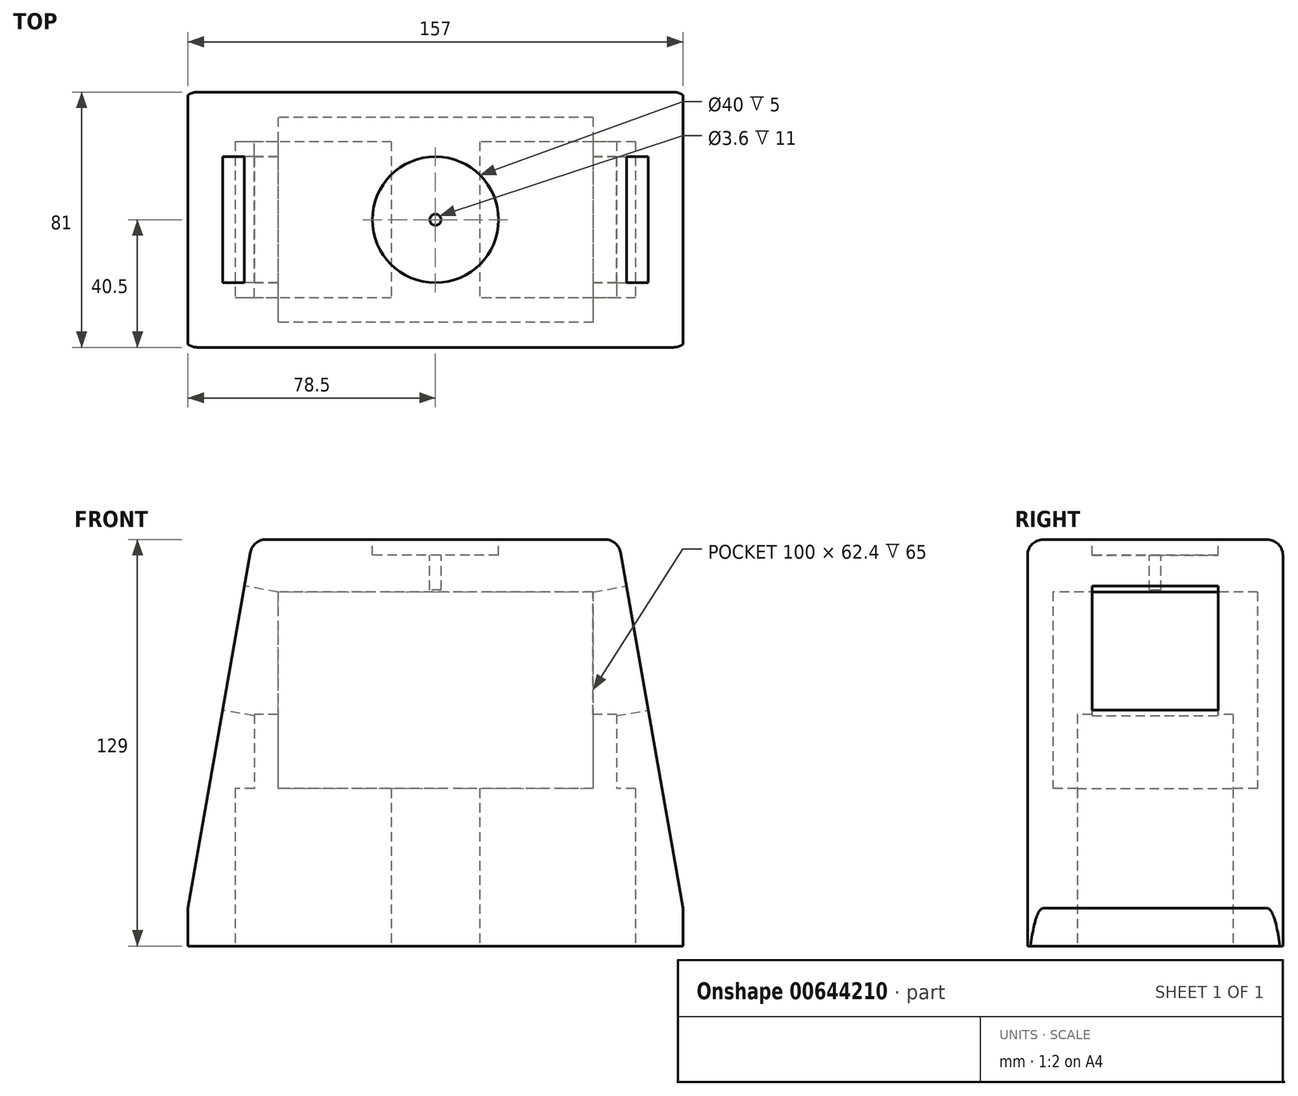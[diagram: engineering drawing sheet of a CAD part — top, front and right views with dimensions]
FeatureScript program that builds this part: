
annotation { "Feature Type Name" : "Feature", "Feature Type Description" : "" }
export const myFeature = defineFeature(function(context is Context, id is Id, definition is map)
    precondition{}
    {
        {
            var Q0;
            Q0=qCreatedBy(makeId("Top.planeOp"),FACE);
            var sketch = newSketch(context, id + "F0", { "sketchPlane" : qUnion([Q0])});
            skLineSegment(sketch, "E0.bottom", {"start": v(78.5, -40.5) * mm, "end": v(-78.5, -40.5) * mm});
            skLineSegment(sketch, "E0.top", {"start": v(78.5, 40.5) * mm, "end": v(-78.5, 40.5) * mm});
            skLineSegment(sketch, "E0.left", {"start": v(78.5, -40.5) * mm, "end": v(78.5, 40.5) * mm});
            skLineSegment(sketch, "E0.right", {"start": v(-78.5, -40.5) * mm, "end": v(-78.5, 40.5) * mm});
            skPoint(sketch, "E0.middle", {"position": v(0, 0) * mm});
            skSolve(sketch);
        }
        {
            var Q0;
            Q0=makeQuery(id+"F0.imprint","IMPRINT",FACE,{"disambiguationData":[TD([[makeQuery(id+"F0.imprint","IMPRINT",EDGE,{"derivedFrom":sQuery(id+"F0.wireOp",EDGE,"E0.bottom")}),-1.0]])]});
            extrude(context, id + "F1", {"entities" : qUnion([Q0]), "depth" : 12 * mm, "offsetDistance" : 25 * mm});
        }
        {
            var Q0;
            Q0=makeQuery(id+"F1.opExtrude","CAP_FACE",FACE,{"disambiguationData":[OSD([sQuery(id+"F0.wireOp",EDGE,"E0.bottom"),sQuery(id+"F0.wireOp",EDGE,"E0.top"),sQuery(id+"F0.wireOp",EDGE,"E0.left"),sQuery(id+"F0.wireOp",EDGE,"E0.right")])],"isStart":false});
            cPlane(context, id + "F2", {"entities" : qUnion([Q0]), "cplaneType" : CPlaneType.OFFSET, "offset" : 117 * mm, "width" : 150 * mm, "height" : 150 * mm});
        }
        {
            var Q0;
            Q0=qCreatedBy(id+"F2.planeOp",FACE);
            var sketch = newSketch(context, id + "F3", { "sketchPlane" : qUnion([Q0])});
            skLineSegment(sketch, "E1.bottom", {"start": v(58, -40.5) * mm, "end": v(-58, -40.5) * mm});
            skLineSegment(sketch, "E1.top", {"start": v(58, 40.5) * mm, "end": v(-58, 40.5) * mm});
            skLineSegment(sketch, "E1.left", {"start": v(58, -40.5) * mm, "end": v(58, 40.5) * mm});
            skLineSegment(sketch, "E1.right", {"start": v(-58, -40.5) * mm, "end": v(-58, 40.5) * mm});
            skPoint(sketch, "E1.middle", {"position": v(0, 0) * mm});
            skSolve(sketch);
        }
        {
            var Q1;
            Q1=makeQuery(id+"F1.opExtrude","CAP_FACE",FACE,{"disambiguationData":[OSD([sQuery(id+"F0.wireOp",EDGE,"E0.bottom"),sQuery(id+"F0.wireOp",EDGE,"E0.top"),sQuery(id+"F0.wireOp",EDGE,"E0.left"),sQuery(id+"F0.wireOp",EDGE,"E0.right")])],"isStart":false});
            var Q2;
            Q2=makeQuery(id+"F3.imprint","IMPRINT",FACE,{"disambiguationData":[TD([[makeQuery(id+"F3.imprint","IMPRINT",EDGE,{"derivedFrom":sQuery(id+"F3.wireOp",EDGE,"E1.bottom")}),-1.0]])]});
            loft(context, id + "F4", {"operationType" : NewBodyOperationType.ADD, "sheetProfilesArray" : [{ "sheetProfileEntities" : qUnion([Q1]) }, { "sheetProfileEntities" : qUnion([Q2]) }]});
        }
        {
            var Q0;
            Q0=makeQuery(id+"F1.opExtrude","CAP_FACE",FACE,{"disambiguationData":[OSD([sQuery(id+"F0.wireOp",EDGE,"E0.bottom"),sQuery(id+"F0.wireOp",EDGE,"E0.top"),sQuery(id+"F0.wireOp",EDGE,"E0.left"),sQuery(id+"F0.wireOp",EDGE,"E0.right")])],"isStart":true});
            var sketch = newSketch(context, id + "F5", { "sketchPlane" : qUnion([Q0])});
            skPoint(sketch, "E2", {"position": v(-38.75, 0) * mm});
            skPoint(sketch, "E3", {"position": v(38.75, 0) * mm});
            skLineSegment(sketch, "E4.bottom", {"start": v(-14, -24.75) * mm, "end": v(-63.5, -24.75) * mm});
            skLineSegment(sketch, "E4.top", {"start": v(-14, 24.75) * mm, "end": v(-63.5, 24.75) * mm});
            skLineSegment(sketch, "E4.left", {"start": v(-14, -24.75) * mm, "end": v(-14, 24.75) * mm});
            skLineSegment(sketch, "E4.right", {"start": v(-63.5, -24.75) * mm, "end": v(-63.5, 24.75) * mm});
            skLineSegment(sketch, "E5.bottom", {"start": v(63.5, -24.75) * mm, "end": v(14, -24.75) * mm});
            skLineSegment(sketch, "E5.top", {"start": v(63.5, 24.75) * mm, "end": v(14, 24.75) * mm});
            skLineSegment(sketch, "E5.left", {"start": v(63.5, -24.75) * mm, "end": v(63.5, 24.75) * mm});
            skLineSegment(sketch, "E5.right", {"start": v(14, -24.75) * mm, "end": v(14, 24.75) * mm});
            skPoint(sketch, "E6.middle", {"position": v(0, 0) * mm});
            skSolve(sketch);
        }
        {
            var Q0;
            Q0=makeQuery(id+"F5.imprint","IMPRINT",FACE,{"disambiguationData":[TD([[makeQuery(id+"F5.imprint","IMPRINT",EDGE,{"derivedFrom":sQuery(id+"F5.wireOp",EDGE,"E4.bottom")}),-1.0]])]});
            var Q1;
            Q1=makeQuery(id+"F5.imprint","IMPRINT",FACE,{"disambiguationData":[TD([[makeQuery(id+"F5.imprint","IMPRINT",EDGE,{"derivedFrom":sQuery(id+"F5.wireOp",EDGE,"E5.bottom")}),-1.0]])]});
            extrude(context, id + "F6", {"entities" : qUnion([Q0, Q1]), "operationType" : NewBodyOperationType.REMOVE, "oppositeDirection" : true, "depth" : 50 * mm, "offsetDistance" : 25 * mm});
        }
        {
            var Q0;
            Q0=makeQuery(id+"F6.boolean.opBoolean","COPY",FACE,{"derivedFrom":makeQuery(id+"F6.opExtrude","CAP_FACE",FACE,{"disambiguationData":[OSD([sQuery(id+"F5.wireOp",EDGE,"E4.bottom"),sQuery(id+"F5.wireOp",EDGE,"E4.top"),sQuery(id+"F5.wireOp",EDGE,"E4.left"),sQuery(id+"F5.wireOp",EDGE,"E4.right")])],"isStart":false})});
            var sketch = newSketch(context, id + "F7", { "sketchPlane" : qUnion([Q0])});
            skLineSegment(sketch, "E7.bottom", {"start": v(50, -32.5) * mm, "end": v(-50, -32.5) * mm});
            skLineSegment(sketch, "E7.top", {"start": v(50, 32.5) * mm, "end": v(-50, 32.5) * mm});
            skLineSegment(sketch, "E7.left", {"start": v(50, -32.5) * mm, "end": v(50, 32.5) * mm});
            skLineSegment(sketch, "E7.right", {"start": v(-50, -32.5) * mm, "end": v(-50, 32.5) * mm});
            skPoint(sketch, "E7.middle", {"position": v(0, 0) * mm});
            skSolve(sketch);
        }
        {
            var Q0;
            {var subQ5=makeQuery(id+"F6.boolean.opBoolean","COPY",EDGE,{"derivedFrom":makeQuery(id+"F6.opExtrude","CAP_EDGE",EDGE,{"disambiguationData":[OSD([sQuery(id+"F5.wireOp",EDGE,"E4.left")])],"isStart":false})});Q0=makeQuery(id+"F7.imprint","IMPRINT",FACE,{"disambiguationData":[TD([[makeQuery(id+"F7.imprint","IMPRINT",EDGE,{"derivedFrom":subQ5}),1.0]])]});}
            var Q1;
            {var subQ1=sQuery(id+"F7.wireOp",EDGE,"E7.bottom");Q1=makeQuery(id+"F7.imprint","IMPRINT",FACE,{"disambiguationData":[TD([[makeQuery(id+"F7.imprint","IMPRINT",EDGE,{"derivedFrom":subQ1}),-1.0]])]});}
            extrude(context, id + "F8", {"entities" : qUnion([Q0, Q1]), "operationType" : NewBodyOperationType.REMOVE, "oppositeDirection" : true, "depth" : 62.4 * mm, "offsetDistance" : 25 * mm});
        }
        {
            var Q0;
            Q0=makeQuery(id+"F4.opLoft","SWEPT_FACE",FACE,{"disambiguationData":[OSD([sQuery(id+"F0.wireOp",EDGE,"E0.bottom"),sQuery(id+"F0.wireOp",EDGE,"E0.top"),sQuery(id+"F0.wireOp",EDGE,"E0.left"),sQuery(id+"F3.wireOp",EDGE,"E1.bottom"),sQuery(id+"F3.wireOp",EDGE,"E1.top"),sQuery(id+"F3.wireOp",EDGE,"E1.left")])]});
            var sketch = newSketch(context, id + "F9", { "sketchPlane" : qUnion([Q0])});
            skLineSegment(sketch, "E8.bottom", {"start": v(25, 57.05) * mm, "end": v(-25, 57.05) * mm});
            skLineSegment(sketch, "E8.top", {"start": v(25, 107.05) * mm, "end": v(-25, 107.05) * mm});
            skLineSegment(sketch, "E8.left", {"start": v(25, 57.05) * mm, "end": v(25, 107.05) * mm});
            skLineSegment(sketch, "E8.right", {"start": v(-25, 57.05) * mm, "end": v(-25, 107.05) * mm});
            skPoint(sketch, "E8.middle", {"position": v(0, 82.05) * mm});
            skPoint(sketch, "E8.middle.positionSnap0", {"position": v(0, 117.05) * mm});
            skPoint(sketch, "E8.centerSnap0", {"position": v(0, 117.05) * mm});
            skSolve(sketch);
        }
        {
            var Q0;
            Q0=makeQuery(id+"F9.imprint","IMPRINT",FACE,{"disambiguationData":[TD([[makeQuery(id+"F9.imprint","IMPRINT",EDGE,{"derivedFrom":sQuery(id+"F9.wireOp",EDGE,"E8.bottom")}),-1.0]])]});
            extrude(context, id + "F10", {"entities" : qUnion([Q0]), "operationType" : NewBodyOperationType.REMOVE, "oppositeDirection" : true, "depth" : 10 * mm, "offsetDistance" : 25 * mm});
        }
        {
            var Q0;
            Q0=makeQuery(id+"F10.boolean.opBoolean","COPY",FACE,{"derivedFrom":makeQuery(id+"F10.opExtrude","CAP_FACE",FACE,{"disambiguationData":[OSD([sQuery(id+"F9.wireOp",EDGE,"E8.bottom"),sQuery(id+"F9.wireOp",EDGE,"E8.top"),sQuery(id+"F9.wireOp",EDGE,"E8.left"),sQuery(id+"F9.wireOp",EDGE,"E8.right")])],"isStart":false})});
            var sketch = newSketch(context, id + "F11", { "sketchPlane" : qUnion([Q0])});
            skLineSegment(sketch, "E9.bottom", {"start": v(20, 62.05) * mm, "end": v(-20, 62.05) * mm});
            skLineSegment(sketch, "E9.top", {"start": v(20, 102.05) * mm, "end": v(-20, 102.05) * mm});
            skLineSegment(sketch, "E9.left", {"start": v(20, 62.05) * mm, "end": v(20, 102.05) * mm});
            skLineSegment(sketch, "E9.right", {"start": v(-20, 62.05) * mm, "end": v(-20, 102.05) * mm});
            skPoint(sketch, "E9.middle", {"position": v(0, 82.05) * mm});
            skPoint(sketch, "E9.middle.positionSnap0", {"position": v(25, 82.05) * mm});
            skPoint(sketch, "E9.middle.positionSnap1", {"position": v(0, 107.05) * mm});
            skPoint(sketch, "E9.centerSnap0", {"position": v(25, 82.05) * mm});
            skPoint(sketch, "E9.centerSnap1", {"position": v(0, 107.05) * mm});
            skSolve(sketch);
        }
        {
            var Q0;
            Q0=makeQuery(id+"F11.imprint","IMPRINT",FACE,{"disambiguationData":[TD([[makeQuery(id+"F11.imprint","IMPRINT",EDGE,{"derivedFrom":sQuery(id+"F11.wireOp",EDGE,"E9.bottom")}),-1.0]])]});
            extrude(context, id + "F12", {"entities" : qUnion([Q0]), "operationType" : NewBodyOperationType.REMOVE, "oppositeDirection" : true, "depth" : 25 * mm, "offsetDistance" : 25 * mm});
        }
        {
            var Q0;
            Q0=makeQuery(id+"F10.boolean.opBoolean","COPY",FACE,{"derivedFrom":makeQuery(id+"F10.opExtrude","CAP_FACE",FACE,{"disambiguationData":[OSD([sQuery(id+"F9.wireOp",EDGE,"E8.bottom"),sQuery(id+"F9.wireOp",EDGE,"E8.top"),sQuery(id+"F9.wireOp",EDGE,"E8.left"),sQuery(id+"F9.wireOp",EDGE,"E8.right")])],"isStart":false})});
            var sketch = newSketch(context, id + "F13", { "sketchPlane" : qUnion([Q0])});
            skLineSegment(sketch, "E10.bottom", {"start": v(25, 57.05) * mm, "end": v(-25, 57.05) * mm});
            skLineSegment(sketch, "E10.top", {"start": v(25, 107.05) * mm, "end": v(-25, 107.05) * mm});
            skLineSegment(sketch, "E10.left", {"start": v(25, 57.05) * mm, "end": v(25, 107.05) * mm});
            skLineSegment(sketch, "E10.right", {"start": v(-25, 57.05) * mm, "end": v(-25, 107.05) * mm});
            skPoint(sketch, "E10.middle", {"position": v(0, 82.05) * mm});
            skPoint(sketch, "E10.middle.positionSnap0", {"position": v(20, 82.05) * mm});
            skPoint(sketch, "E10.middle.positionSnap1", {"position": v(0, 102.05) * mm});
            skPoint(sketch, "E10.centerSnap0", {"position": v(20, 82.05) * mm});
            skPoint(sketch, "E10.centerSnap1", {"position": v(0, 102.05) * mm});
            skSolve(sketch);
        }
        {
            var Q0;
            Q0=makeQuery(id+"F13.imprint","IMPRINT",FACE,{"disambiguationData":[TD([[makeQuery(id+"F13.imprint","IMPRINT",EDGE,{"derivedFrom":sQuery(id+"F13.wireOp",EDGE,"E10.bottom")}),-1.0]])]});
            var Q1;
            Q1=makeQuery(id+"F13.imprint","IMPRINT",FACE,{"disambiguationData":[TD([[makeQuery(id+"F13.imprint","IMPRINT",EDGE,{"derivedFrom":makeQuery(id+"F12.boolean.opBoolean","COPY",EDGE,{"derivedFrom":makeQuery(id+"F12.opExtrude","CAP_EDGE",EDGE,{"disambiguationData":[OSD([sQuery(id+"F11.wireOp",EDGE,"E9.bottom")])],"isStart":true})})}),-1.0]])]});
            extrude(context, id + "F14", {"entities" : qUnion([Q0, Q1]), "operationType" : NewBodyOperationType.ADD, "depth" : 10 * mm, "offsetDistance" : 25 * mm});
        }
        {
            var Q0;
            Q0=makeQuery(id+"F14.boolean.opBoolean","MERGE",FACE,{"derivedFrom":[makeQuery(id+"F4.opLoft","SWEPT_FACE",FACE,{"disambiguationData":[OSD([sQuery(id+"F0.wireOp",EDGE,"E0.bottom"),sQuery(id+"F0.wireOp",EDGE,"E0.top"),sQuery(id+"F0.wireOp",EDGE,"E0.left"),sQuery(id+"F3.wireOp",EDGE,"E1.bottom"),sQuery(id+"F3.wireOp",EDGE,"E1.top"),sQuery(id+"F3.wireOp",EDGE,"E1.left")])]}),makeQuery(id+"F14.opExtrude","CAP_FACE",FACE,{"disambiguationData":[OSD([sQuery(id+"F13.wireOp",EDGE,"E10.bottom"),sQuery(id+"F13.wireOp",EDGE,"E10.top"),sQuery(id+"F13.wireOp",EDGE,"E10.left"),sQuery(id+"F13.wireOp",EDGE,"E10.right")])],"isStart":false})]});
            var sketch = newSketch(context, id + "F15", { "sketchPlane" : qUnion([Q0])});
            skPoint(sketch, "E11", {"position": v(0, 82.05) * mm});
            skPoint(sketch, "E11.positionSnap0", {"position": v(0, 117.05) * mm});
            skCircle(sketch, "E12", {"center": v(0, 82.05) * mm, "radius": 12.5 * mm});
            skCircle(sketch, "E13", {"center": v(0, 82.05) * mm, "radius": 17.5 * mm});
            skLineSegment(sketch, "E14.bottom", {"start": v(-2.5, 82.05) * mm, "end": v(2.5, 82.05) * mm});
            skLineSegment(sketch, "E14.top", {"start": v(-2.5, 101.72) * mm, "end": v(2.5, 101.72) * mm});
            skLineSegment(sketch, "E14.left", {"start": v(-2.5, 82.05) * mm, "end": v(-2.5, 101.72) * mm});
            skLineSegment(sketch, "E14.right", {"start": v(2.5, 82.05) * mm, "end": v(2.5, 101.72) * mm});
            skLineSegment(sketch, "E15.1.0", {"start": v(-2.02, 80.58) * mm, "end": v(-13.58, 96.5) * mm});
            skLineSegment(sketch, "E15.1.1", {"start": v(2.02, 83.52) * mm, "end": v(-9.54, 99.43) * mm});
            skLineSegment(sketch, "E15.1.2", {"start": v(-13.58, 96.5) * mm, "end": v(-9.54, 99.43) * mm});
            skLineSegment(sketch, "E15.1.3", {"start": v(-2.02, 80.58) * mm, "end": v(2.02, 83.52) * mm});
            skLineSegment(sketch, "E15.2.0", {"start": v(-0.77, 79.68) * mm, "end": v(-19.48, 85.75) * mm});
            skLineSegment(sketch, "E15.2.1", {"start": v(0.77, 84.43) * mm, "end": v(-17.93, 90.5) * mm});
            skLineSegment(sketch, "E15.2.2", {"start": v(-19.48, 85.75) * mm, "end": v(-17.93, 90.5) * mm});
            skLineSegment(sketch, "E15.2.3", {"start": v(-0.77, 79.68) * mm, "end": v(0.77, 84.43) * mm});
            skLineSegment(sketch, "E15.3.0", {"start": v(0.77, 79.68) * mm, "end": v(-17.93, 73.6) * mm});
            skLineSegment(sketch, "E15.3.1", {"start": v(-0.77, 84.43) * mm, "end": v(-19.48, 78.36) * mm});
            skLineSegment(sketch, "E15.3.2", {"start": v(-17.93, 73.6) * mm, "end": v(-19.48, 78.36) * mm});
            skLineSegment(sketch, "E15.3.3", {"start": v(0.77, 79.68) * mm, "end": v(-0.77, 84.43) * mm});
            skLineSegment(sketch, "E15.4.0", {"start": v(2.02, 80.58) * mm, "end": v(-9.54, 64.68) * mm});
            skLineSegment(sketch, "E15.4.1", {"start": v(-2.02, 83.52) * mm, "end": v(-13.58, 67.61) * mm});
            skLineSegment(sketch, "E15.4.2", {"start": v(-9.54, 64.68) * mm, "end": v(-13.58, 67.61) * mm});
            skLineSegment(sketch, "E15.4.3", {"start": v(2.02, 80.58) * mm, "end": v(-2.02, 83.52) * mm});
            skLineSegment(sketch, "E15.5.0", {"start": v(2.5, 82.05) * mm, "end": v(2.5, 62.39) * mm});
            skLineSegment(sketch, "E15.5.1", {"start": v(-2.5, 82.05) * mm, "end": v(-2.5, 62.39) * mm});
            skLineSegment(sketch, "E15.5.2", {"start": v(2.5, 62.39) * mm, "end": v(-2.5, 62.39) * mm});
            skLineSegment(sketch, "E15.5.3", {"start": v(2.5, 82.05) * mm, "end": v(-2.5, 82.05) * mm});
            skLineSegment(sketch, "E15.6.0", {"start": v(2.02, 83.52) * mm, "end": v(13.58, 67.61) * mm});
            skLineSegment(sketch, "E15.6.1", {"start": v(-2.02, 80.58) * mm, "end": v(9.54, 64.68) * mm});
            skLineSegment(sketch, "E15.6.2", {"start": v(13.58, 67.61) * mm, "end": v(9.54, 64.68) * mm});
            skLineSegment(sketch, "E15.6.3", {"start": v(2.02, 83.52) * mm, "end": v(-2.02, 80.58) * mm});
            skLineSegment(sketch, "E15.7.0", {"start": v(0.77, 84.43) * mm, "end": v(19.48, 78.36) * mm});
            skLineSegment(sketch, "E15.7.1", {"start": v(-0.77, 79.68) * mm, "end": v(17.93, 73.6) * mm});
            skLineSegment(sketch, "E15.7.2", {"start": v(19.48, 78.36) * mm, "end": v(17.93, 73.6) * mm});
            skLineSegment(sketch, "E15.7.3", {"start": v(0.77, 84.43) * mm, "end": v(-0.77, 79.68) * mm});
            skLineSegment(sketch, "E15.8.0", {"start": v(-0.77, 84.43) * mm, "end": v(17.93, 90.5) * mm});
            skLineSegment(sketch, "E15.8.1", {"start": v(0.77, 79.68) * mm, "end": v(19.48, 85.75) * mm});
            skLineSegment(sketch, "E15.8.2", {"start": v(17.93, 90.5) * mm, "end": v(19.48, 85.75) * mm});
            skLineSegment(sketch, "E15.8.3", {"start": v(-0.77, 84.43) * mm, "end": v(0.77, 79.68) * mm});
            skLineSegment(sketch, "E15.9.0", {"start": v(-2.02, 83.52) * mm, "end": v(9.54, 99.43) * mm});
            skLineSegment(sketch, "E15.9.1", {"start": v(2.02, 80.58) * mm, "end": v(13.58, 96.5) * mm});
            skLineSegment(sketch, "E15.9.2", {"start": v(9.54, 99.43) * mm, "end": v(13.58, 96.5) * mm});
            skLineSegment(sketch, "E15.9.3", {"start": v(-2.02, 83.52) * mm, "end": v(2.02, 80.58) * mm});
            skSolve(sketch);
        }
        {
            var Q0;
            {var subQ0=sQuery(id+"F15.wireOp",EDGE,"E14.right");var subQ1=sQuery(id+"F15.wireOp",EDGE,"E12");var subQ2=makeQuery(id+"F15.imprint","INTERSECT",VERTEX,{"derivedFrom":[subQ1,subQ0]});Q0=makeQuery(id+"F15.imprint","IMPRINT",FACE,{"disambiguationData":[TD([[makeQuery(id+"F15.imprint","IMPRINT",EDGE,{"disambiguationData":[TD([[subQ2,-1.0]])],"derivedFrom":subQ1}),-1.0]])]});}
            var Q1;
            {var subQ0=sQuery(id+"F15.wireOp",EDGE,"E14.right");var subQ1=sQuery(id+"F15.wireOp",EDGE,"E12");var subQ2=makeQuery(id+"F15.imprint","INTERSECT",VERTEX,{"derivedFrom":[subQ1,subQ0]});Q1=makeQuery(id+"F15.imprint","IMPRINT",FACE,{"disambiguationData":[TD([[makeQuery(id+"F15.imprint","IMPRINT",EDGE,{"disambiguationData":[TD([[subQ2,-1.0]])],"derivedFrom":subQ1}),1.0]])]});}
            var Q2;
            {var subQ0=sQuery(id+"F15.wireOp",EDGE,"E15.4.1");var subQ1=sQuery(id+"F15.wireOp",EDGE,"E12");var subQ2=makeQuery(id+"F15.imprint","INTERSECT",VERTEX,{"derivedFrom":[subQ1,subQ0]});Q2=makeQuery(id+"F15.imprint","IMPRINT",FACE,{"disambiguationData":[TD([[makeQuery(id+"F15.imprint","IMPRINT",EDGE,{"disambiguationData":[TD([[subQ2,-1.0]])],"derivedFrom":subQ1}),1.0]])]});}
            var Q3;
            {var subQ0=sQuery(id+"F15.wireOp",EDGE,"E15.4.1");var subQ1=sQuery(id+"F15.wireOp",EDGE,"E12");var subQ2=makeQuery(id+"F15.imprint","INTERSECT",VERTEX,{"derivedFrom":[subQ1,subQ0]});Q3=makeQuery(id+"F15.imprint","IMPRINT",FACE,{"disambiguationData":[TD([[makeQuery(id+"F15.imprint","IMPRINT",EDGE,{"disambiguationData":[TD([[subQ2,-1.0]])],"derivedFrom":subQ1}),-1.0]])]});}
            var Q4;
            {var subQ0=sQuery(id+"F15.wireOp",EDGE,"E15.6.1");var subQ1=sQuery(id+"F15.wireOp",EDGE,"E12");var subQ2=makeQuery(id+"F15.imprint","INTERSECT",VERTEX,{"derivedFrom":[subQ1,subQ0]});Q4=makeQuery(id+"F15.imprint","IMPRINT",FACE,{"disambiguationData":[TD([[makeQuery(id+"F15.imprint","IMPRINT",EDGE,{"disambiguationData":[TD([[subQ2,-1.0]])],"derivedFrom":subQ1}),-1.0]])]});}
            var Q5;
            {var subQ0=sQuery(id+"F15.wireOp",EDGE,"E15.6.1");var subQ1=sQuery(id+"F15.wireOp",EDGE,"E12");var subQ2=makeQuery(id+"F15.imprint","INTERSECT",VERTEX,{"derivedFrom":[subQ1,subQ0]});Q5=makeQuery(id+"F15.imprint","IMPRINT",FACE,{"disambiguationData":[TD([[makeQuery(id+"F15.imprint","IMPRINT",EDGE,{"disambiguationData":[TD([[subQ2,-1.0]])],"derivedFrom":subQ1}),1.0]])]});}
            var Q6;
            {var subQ0=sQuery(id+"F15.wireOp",EDGE,"E15.5.1");var subQ1=sQuery(id+"F15.wireOp",EDGE,"E12");var subQ2=makeQuery(id+"F15.imprint","INTERSECT",VERTEX,{"derivedFrom":[subQ1,subQ0]});Q6=makeQuery(id+"F15.imprint","IMPRINT",FACE,{"disambiguationData":[TD([[makeQuery(id+"F15.imprint","IMPRINT",EDGE,{"disambiguationData":[TD([[subQ2,-1.0]])],"derivedFrom":subQ1}),1.0]])]});}
            var Q7;
            {var subQ0=sQuery(id+"F15.wireOp",EDGE,"E15.4.0");var subQ1=sQuery(id+"F15.wireOp",EDGE,"E12");var subQ2=makeQuery(id+"F15.imprint","INTERSECT",VERTEX,{"derivedFrom":[subQ1,subQ0]});Q7=makeQuery(id+"F15.imprint","IMPRINT",FACE,{"disambiguationData":[TD([[makeQuery(id+"F15.imprint","IMPRINT",EDGE,{"disambiguationData":[TD([[subQ2,-1.0]])],"derivedFrom":subQ1}),1.0]])]});}
            var Q8;
            {var subQ0=sQuery(id+"F15.wireOp",EDGE,"E15.5.0");var subQ1=sQuery(id+"F15.wireOp",EDGE,"E12");var subQ2=makeQuery(id+"F15.imprint","INTERSECT",VERTEX,{"derivedFrom":[subQ1,subQ0]});Q8=makeQuery(id+"F15.imprint","IMPRINT",FACE,{"disambiguationData":[TD([[makeQuery(id+"F15.imprint","IMPRINT",EDGE,{"disambiguationData":[TD([[subQ2,-1.0]])],"derivedFrom":subQ1}),1.0]])]});}
            var Q9;
            {var subQ0=sQuery(id+"F15.wireOp",EDGE,"E15.6.0");var subQ1=sQuery(id+"F15.wireOp",EDGE,"E12");var subQ2=makeQuery(id+"F15.imprint","INTERSECT",VERTEX,{"derivedFrom":[subQ1,subQ0]});Q9=makeQuery(id+"F15.imprint","IMPRINT",FACE,{"disambiguationData":[TD([[makeQuery(id+"F15.imprint","IMPRINT",EDGE,{"disambiguationData":[TD([[subQ2,-1.0]])],"derivedFrom":subQ1}),1.0]])]});}
            var Q10;
            {var subQ0=sQuery(id+"F15.wireOp",EDGE,"E15.7.1");var subQ1=sQuery(id+"F15.wireOp",EDGE,"E12");var subQ2=makeQuery(id+"F15.imprint","INTERSECT",VERTEX,{"derivedFrom":[subQ1,subQ0]});Q10=makeQuery(id+"F15.imprint","IMPRINT",FACE,{"disambiguationData":[TD([[makeQuery(id+"F15.imprint","IMPRINT",EDGE,{"disambiguationData":[TD([[subQ2,-1.0]])],"derivedFrom":subQ1}),1.0]])]});}
            var Q11;
            {var subQ0=sQuery(id+"F15.wireOp",EDGE,"E15.8.1");var subQ1=sQuery(id+"F15.wireOp",EDGE,"E12");var subQ2=makeQuery(id+"F15.imprint","INTERSECT",VERTEX,{"derivedFrom":[subQ1,subQ0]});Q11=makeQuery(id+"F15.imprint","IMPRINT",FACE,{"disambiguationData":[TD([[makeQuery(id+"F15.imprint","IMPRINT",EDGE,{"disambiguationData":[TD([[subQ2,1.0]])],"derivedFrom":subQ1}),1.0]])]});}
            var Q12;
            {var subQ1=sQuery(id+"F15.wireOp",EDGE,"E12");var subQ7=sQuery(id+"F15.wireOp",EDGE,"E15.8.0");var subQ8=makeQuery(id+"F15.imprint","INTERSECT",VERTEX,{"derivedFrom":[subQ1,subQ7]});Q12=makeQuery(id+"F15.imprint","IMPRINT",FACE,{"disambiguationData":[TD([[makeQuery(id+"F15.imprint","IMPRINT",EDGE,{"disambiguationData":[TD([[subQ8,1.0]])],"derivedFrom":subQ1}),1.0]])]});}
            var Q13;
            {var subQ3=sQuery(id+"F15.wireOp",EDGE,"E15.9.1");var subQ7=sQuery(id+"F15.wireOp",EDGE,"E12");var subQ8=makeQuery(id+"F15.imprint","INTERSECT",VERTEX,{"derivedFrom":[subQ7,subQ3]});Q13=makeQuery(id+"F15.imprint","IMPRINT",FACE,{"disambiguationData":[TD([[makeQuery(id+"F15.imprint","IMPRINT",EDGE,{"disambiguationData":[TD([[subQ8,-1.0]])],"derivedFrom":subQ7}),1.0]])]});}
            var Q14;
            {var subQ0=sQuery(id+"F15.wireOp",EDGE,"E15.8.0");var subQ1=sQuery(id+"F15.wireOp",EDGE,"E12");var subQ2=makeQuery(id+"F15.imprint","INTERSECT",VERTEX,{"derivedFrom":[subQ1,subQ0]});Q14=makeQuery(id+"F15.imprint","IMPRINT",FACE,{"disambiguationData":[TD([[makeQuery(id+"F15.imprint","IMPRINT",EDGE,{"disambiguationData":[TD([[subQ2,-1.0]])],"derivedFrom":subQ1}),1.0]])]});}
            var Q15;
            {var subQ0=sQuery(id+"F15.wireOp",EDGE,"E15.9.0");var subQ1=sQuery(id+"F15.wireOp",EDGE,"E12");var subQ2=makeQuery(id+"F15.imprint","INTERSECT",VERTEX,{"derivedFrom":[subQ1,subQ0]});Q15=makeQuery(id+"F15.imprint","IMPRINT",FACE,{"disambiguationData":[TD([[makeQuery(id+"F15.imprint","IMPRINT",EDGE,{"disambiguationData":[TD([[subQ2,-1.0]])],"derivedFrom":subQ1}),1.0]])]});}
            var Q16;
            {var subQ0=sQuery(id+"F15.wireOp",EDGE,"E14.left");var subQ1=sQuery(id+"F15.wireOp",EDGE,"E12");var subQ2=makeQuery(id+"F15.imprint","INTERSECT",VERTEX,{"derivedFrom":[subQ1,subQ0]});Q16=makeQuery(id+"F15.imprint","IMPRINT",FACE,{"disambiguationData":[TD([[makeQuery(id+"F15.imprint","IMPRINT",EDGE,{"disambiguationData":[TD([[subQ2,-1.0]])],"derivedFrom":subQ1}),1.0]])]});}
            var Q17;
            {var subQ1=sQuery(id+"F15.wireOp",EDGE,"E12");var subQ7=sQuery(id+"F15.wireOp",EDGE,"E15.1.1");var subQ9=makeQuery(id+"F15.imprint","INTERSECT",VERTEX,{"derivedFrom":[subQ1,subQ7]});Q17=makeQuery(id+"F15.imprint","IMPRINT",FACE,{"disambiguationData":[TD([[makeQuery(id+"F15.imprint","IMPRINT",EDGE,{"disambiguationData":[TD([[subQ9,-1.0]])],"derivedFrom":subQ1}),1.0]])]});}
            var Q18;
            {var subQ0=sQuery(id+"F15.wireOp",EDGE,"E15.1.0");var subQ1=sQuery(id+"F15.wireOp",EDGE,"E12");var subQ2=makeQuery(id+"F15.imprint","INTERSECT",VERTEX,{"derivedFrom":[subQ1,subQ0]});Q18=makeQuery(id+"F15.imprint","IMPRINT",FACE,{"disambiguationData":[TD([[makeQuery(id+"F15.imprint","IMPRINT",EDGE,{"disambiguationData":[TD([[subQ2,-1.0]])],"derivedFrom":subQ1}),1.0]])]});}
            var Q19;
            {var subQ0=sQuery(id+"F15.wireOp",EDGE,"E15.2.1");var subQ1=sQuery(id+"F15.wireOp",EDGE,"E12");var subQ2=makeQuery(id+"F15.imprint","INTERSECT",VERTEX,{"derivedFrom":[subQ1,subQ0]});Q19=makeQuery(id+"F15.imprint","IMPRINT",FACE,{"disambiguationData":[TD([[makeQuery(id+"F15.imprint","IMPRINT",EDGE,{"disambiguationData":[TD([[subQ2,-1.0]])],"derivedFrom":subQ1}),1.0]])]});}
            var Q20;
            {var subQ0=sQuery(id+"F15.wireOp",EDGE,"E15.2.0");var subQ1=sQuery(id+"F15.wireOp",EDGE,"E12");var subQ2=makeQuery(id+"F15.imprint","INTERSECT",VERTEX,{"derivedFrom":[subQ1,subQ0]});Q20=makeQuery(id+"F15.imprint","IMPRINT",FACE,{"disambiguationData":[TD([[makeQuery(id+"F15.imprint","IMPRINT",EDGE,{"disambiguationData":[TD([[subQ2,-1.0]])],"derivedFrom":subQ1}),1.0]])]});}
            var Q21;
            {var subQ0=sQuery(id+"F15.wireOp",EDGE,"E15.3.0");var subQ1=sQuery(id+"F15.wireOp",EDGE,"E12");var subQ2=makeQuery(id+"F15.imprint","INTERSECT",VERTEX,{"derivedFrom":[subQ1,subQ0]});Q21=makeQuery(id+"F15.imprint","IMPRINT",FACE,{"disambiguationData":[TD([[makeQuery(id+"F15.imprint","IMPRINT",EDGE,{"disambiguationData":[TD([[subQ2,-1.0]])],"derivedFrom":subQ1}),1.0]])]});}
            var Q22;
            {var subQ0=sQuery(id+"F15.wireOp",EDGE,"E15.3.1");var subQ1=sQuery(id+"F15.wireOp",EDGE,"E12");var subQ2=makeQuery(id+"F15.imprint","INTERSECT",VERTEX,{"derivedFrom":[subQ1,subQ0]});Q22=makeQuery(id+"F15.imprint","IMPRINT",FACE,{"disambiguationData":[TD([[makeQuery(id+"F15.imprint","IMPRINT",EDGE,{"disambiguationData":[TD([[subQ2,-1.0]])],"derivedFrom":subQ1}),1.0]])]});}
            var Q23;
            {var subQ0=sQuery(id+"F15.wireOp",EDGE,"E15.8.1");var subQ1=sQuery(id+"F15.wireOp",EDGE,"E15.4.0");var subQ2=makeQuery(id+"F15.imprint","INTERSECT",VERTEX,{"derivedFrom":[subQ1,subQ0]});Q23=makeQuery(id+"F15.imprint","IMPRINT",FACE,{"disambiguationData":[TD([[makeQuery(id+"F15.imprint","IMPRINT",EDGE,{"disambiguationData":[TD([[subQ2,-1.0]])],"derivedFrom":subQ1}),1.0]])]});}
            var Q24;
            {var subQ1=sQuery(id+"F15.wireOp",EDGE,"E15.1.1");var subQ3=sQuery(id+"F15.wireOp",EDGE,"E15.7.0");var subQ4=makeQuery(id+"F15.imprint","INTERSECT",VERTEX,{"derivedFrom":[subQ1,subQ3]});Q24=makeQuery(id+"F15.imprint","IMPRINT",FACE,{"disambiguationData":[TD([[makeQuery(id+"F15.imprint","IMPRINT",EDGE,{"disambiguationData":[TD([[subQ4,1.0]])],"derivedFrom":subQ1}),1.0]])]});}
            var Q25;
            {var subQ0=sQuery(id+"F15.wireOp",EDGE,"E15.7.1");var subQ1=sQuery(id+"F15.wireOp",EDGE,"E15.4.0");var subQ2=makeQuery(id+"F15.imprint","INTERSECT",VERTEX,{"derivedFrom":[subQ1,subQ0]});Q25=makeQuery(id+"F15.imprint","IMPRINT",FACE,{"disambiguationData":[TD([[makeQuery(id+"F15.imprint","IMPRINT",EDGE,{"disambiguationData":[TD([[subQ2,-1.0]])],"derivedFrom":subQ1}),1.0]])]});}
            var Q26;
            {var subQ0=sQuery(id+"F15.wireOp",EDGE,"E15.4.1");var subQ1=sQuery(id+"F15.wireOp",EDGE,"E14.left");var subQ2=makeQuery(id+"F15.imprint","INTERSECT",VERTEX,{"derivedFrom":[subQ1,subQ0]});Q26=makeQuery(id+"F15.imprint","IMPRINT",FACE,{"disambiguationData":[TD([[makeQuery(id+"F15.imprint","IMPRINT",EDGE,{"disambiguationData":[TD([[subQ2,-1.0]])],"derivedFrom":subQ1}),1.0]])]});}
            var Q27;
            {var subQ0=sQuery(id+"F15.wireOp",EDGE,"E15.6.0");var subQ1=sQuery(id+"F15.wireOp",EDGE,"E14.right");var subQ2=makeQuery(id+"F15.imprint","INTERSECT",VERTEX,{"derivedFrom":[subQ1,subQ0]});Q27=makeQuery(id+"F15.imprint","IMPRINT",FACE,{"disambiguationData":[TD([[makeQuery(id+"F15.imprint","IMPRINT",EDGE,{"disambiguationData":[TD([[subQ2,-1.0]])],"derivedFrom":subQ1}),-1.0]])]});}
            var Q28;
            {var subQ0=sQuery(id+"F15.wireOp",EDGE,"E15.8.1");var subQ1=sQuery(id+"F15.wireOp",EDGE,"E15.5.0");var subQ2=makeQuery(id+"F15.imprint","INTERSECT",VERTEX,{"derivedFrom":[subQ1,subQ0]});Q28=makeQuery(id+"F15.imprint","IMPRINT",FACE,{"disambiguationData":[TD([[makeQuery(id+"F15.imprint","IMPRINT",EDGE,{"disambiguationData":[TD([[subQ2,-1.0]])],"derivedFrom":subQ1}),1.0]])]});}
            var Q29;
            {var subQ0=sQuery(id+"F15.wireOp",EDGE,"E15.2.1");var subQ1=sQuery(id+"F15.wireOp",EDGE,"E14.left");var subQ2=makeQuery(id+"F15.imprint","INTERSECT",VERTEX,{"derivedFrom":[subQ1,subQ0]});Q29=makeQuery(id+"F15.imprint","IMPRINT",FACE,{"disambiguationData":[TD([[makeQuery(id+"F15.imprint","IMPRINT",EDGE,{"disambiguationData":[TD([[subQ2,-1.0]])],"derivedFrom":subQ1}),-1.0]])]});}
            var Q30;
            {var subQ0=sQuery(id+"F15.wireOp",EDGE,"E15.4.1");var subQ1=sQuery(id+"F15.wireOp",EDGE,"E14.left");var subQ2=makeQuery(id+"F15.imprint","INTERSECT",VERTEX,{"derivedFrom":[subQ1,subQ0]});Q30=makeQuery(id+"F15.imprint","IMPRINT",FACE,{"disambiguationData":[TD([[makeQuery(id+"F15.imprint","IMPRINT",EDGE,{"disambiguationData":[TD([[subQ2,-1.0]])],"derivedFrom":subQ1}),-1.0]])]});}
            var Q31;
            {var subQ0=sQuery(id+"F15.wireOp",EDGE,"E15.7.0");var subQ1=sQuery(id+"F15.wireOp",EDGE,"E15.1.1");var subQ2=makeQuery(id+"F15.imprint","INTERSECT",VERTEX,{"derivedFrom":[subQ1,subQ0]});Q31=makeQuery(id+"F15.imprint","IMPRINT",FACE,{"disambiguationData":[TD([[makeQuery(id+"F15.imprint","IMPRINT",EDGE,{"disambiguationData":[TD([[subQ2,-1.0]])],"derivedFrom":subQ1}),1.0]])]});}
            var Q32;
            {var subQ1=sQuery(id+"F15.wireOp",EDGE,"E15.5.0");var subQ3=sQuery(id+"F15.wireOp",EDGE,"E15.9.1");var subQ4=makeQuery(id+"F15.imprint","INTERSECT",VERTEX,{"derivedFrom":[subQ1,subQ3]});Q32=makeQuery(id+"F15.imprint","IMPRINT",FACE,{"disambiguationData":[TD([[makeQuery(id+"F15.imprint","IMPRINT",EDGE,{"disambiguationData":[TD([[subQ4,1.0]])],"derivedFrom":subQ1}),-1.0]])]});}
            var Q33;
            {var subQ0=sQuery(id+"F15.wireOp",EDGE,"E15.8.0");var subQ1=sQuery(id+"F15.wireOp",EDGE,"E14.right");var subQ2=makeQuery(id+"F15.imprint","INTERSECT",VERTEX,{"derivedFrom":[subQ1,subQ0]});Q33=makeQuery(id+"F15.imprint","IMPRINT",FACE,{"disambiguationData":[TD([[makeQuery(id+"F15.imprint","IMPRINT",EDGE,{"disambiguationData":[TD([[subQ2,-1.0]])],"derivedFrom":subQ1}),1.0]])]});}
            var Q34;
            {var subQ0=sQuery(id+"F15.wireOp",EDGE,"E15.6.1");var subQ5=sQuery(id+"F15.wireOp",EDGE,"E15.2.0");var subQ6=makeQuery(id+"F15.imprint","INTERSECT",VERTEX,{"derivedFrom":[subQ5,subQ0]});Q34=makeQuery(id+"F15.imprint","IMPRINT",FACE,{"disambiguationData":[TD([[makeQuery(id+"F15.imprint","IMPRINT",EDGE,{"disambiguationData":[TD([[subQ6,-1.0]])],"derivedFrom":subQ5}),-1.0]])]});}
            var Q35;
            {var subQ0=sQuery(id+"F15.wireOp",EDGE,"E15.9.1");var subQ1=sQuery(id+"F15.wireOp",EDGE,"E15.5.0");var subQ2=makeQuery(id+"F15.imprint","INTERSECT",VERTEX,{"derivedFrom":[subQ1,subQ0]});Q35=makeQuery(id+"F15.imprint","IMPRINT",FACE,{"disambiguationData":[TD([[makeQuery(id+"F15.imprint","IMPRINT",EDGE,{"disambiguationData":[TD([[subQ2,-1.0]])],"derivedFrom":subQ1}),1.0]])]});}
            var Q36;
            {var subQ1=sQuery(id+"F15.wireOp",EDGE,"E15.3.0");var subQ3=sQuery(id+"F15.wireOp",EDGE,"E15.7.1");var subQ4=makeQuery(id+"F15.imprint","INTERSECT",VERTEX,{"derivedFrom":[subQ1,subQ3]});Q36=makeQuery(id+"F15.imprint","IMPRINT",FACE,{"disambiguationData":[TD([[makeQuery(id+"F15.imprint","IMPRINT",EDGE,{"disambiguationData":[TD([[subQ4,1.0]])],"derivedFrom":subQ1}),-1.0]])]});}
            var Q37;
            {var subQ0=sQuery(id+"F15.wireOp",EDGE,"E15.7.0");var subQ1=sQuery(id+"F15.wireOp",EDGE,"E14.right");var subQ2=makeQuery(id+"F15.imprint","INTERSECT",VERTEX,{"derivedFrom":[subQ1,subQ0]});Q37=makeQuery(id+"F15.imprint","IMPRINT",FACE,{"disambiguationData":[TD([[makeQuery(id+"F15.imprint","IMPRINT",EDGE,{"disambiguationData":[TD([[subQ2,-1.0]])],"derivedFrom":subQ1}),-1.0]])]});}
            var Q38;
            {var subQ0=sQuery(id+"F15.wireOp",EDGE,"E15.6.1");var subQ1=sQuery(id+"F15.wireOp",EDGE,"E15.3.0");var subQ2=makeQuery(id+"F15.imprint","INTERSECT",VERTEX,{"derivedFrom":[subQ1,subQ0]});Q38=makeQuery(id+"F15.imprint","IMPRINT",FACE,{"disambiguationData":[TD([[makeQuery(id+"F15.imprint","IMPRINT",EDGE,{"disambiguationData":[TD([[subQ2,-1.0]])],"derivedFrom":subQ1}),1.0]])]});}
            var Q39;
            {var subQ0=sQuery(id+"F15.wireOp",EDGE,"E15.7.1");var subQ1=sQuery(id+"F15.wireOp",EDGE,"E15.3.0");var subQ2=makeQuery(id+"F15.imprint","INTERSECT",VERTEX,{"derivedFrom":[subQ1,subQ0]});Q39=makeQuery(id+"F15.imprint","IMPRINT",FACE,{"disambiguationData":[TD([[makeQuery(id+"F15.imprint","IMPRINT",EDGE,{"disambiguationData":[TD([[subQ2,-1.0]])],"derivedFrom":subQ1}),1.0]])]});}
            var Q40;
            {var subQ1=sQuery(id+"F15.wireOp",EDGE,"E15.4.0");var subQ3=sQuery(id+"F15.wireOp",EDGE,"E15.8.1");var subQ4=makeQuery(id+"F15.imprint","INTERSECT",VERTEX,{"derivedFrom":[subQ1,subQ3]});Q40=makeQuery(id+"F15.imprint","IMPRINT",FACE,{"disambiguationData":[TD([[makeQuery(id+"F15.imprint","IMPRINT",EDGE,{"disambiguationData":[TD([[subQ4,1.0]])],"derivedFrom":subQ1}),-1.0]])]});}
            var Q41;
            {var subQ1=sQuery(id+"F15.wireOp",EDGE,"E14.right");var subQ3=sQuery(id+"F15.wireOp",EDGE,"E15.6.0");var subQ4=makeQuery(id+"F15.imprint","INTERSECT",VERTEX,{"derivedFrom":[subQ1,subQ3]});Q41=makeQuery(id+"F15.imprint","IMPRINT",FACE,{"disambiguationData":[TD([[makeQuery(id+"F15.imprint","IMPRINT",EDGE,{"disambiguationData":[TD([[subQ4,-1.0]])],"derivedFrom":subQ3}),-1.0]])]});}
            var Q42;
            {var subQ1=sQuery(id+"F15.wireOp",EDGE,"E14.left");var subQ3=sQuery(id+"F15.wireOp",EDGE,"E15.4.1");var subQ4=makeQuery(id+"F15.imprint","INTERSECT",VERTEX,{"derivedFrom":[subQ1,subQ3]});Q42=makeQuery(id+"F15.imprint","IMPRINT",FACE,{"disambiguationData":[TD([[makeQuery(id+"F15.imprint","IMPRINT",EDGE,{"disambiguationData":[TD([[subQ4,1.0]])],"derivedFrom":subQ1}),-1.0]])]});}
            var Q43;
            {var subQ1=sQuery(id+"F15.wireOp",EDGE,"E15.1.0");var subQ3=sQuery(id+"F15.wireOp",EDGE,"E15.5.1");var subQ4=makeQuery(id+"F15.imprint","INTERSECT",VERTEX,{"derivedFrom":[subQ1,subQ3]});Q43=makeQuery(id+"F15.imprint","IMPRINT",FACE,{"disambiguationData":[TD([[makeQuery(id+"F15.imprint","IMPRINT",EDGE,{"disambiguationData":[TD([[subQ4,1.0]])],"derivedFrom":subQ1}),-1.0]])]});}
            var Q44;
            {var subQ0=sQuery(id+"F15.wireOp",EDGE,"E15.5.1");var subQ5=sQuery(id+"F15.wireOp",EDGE,"E15.1.0");var subQ6=makeQuery(id+"F15.imprint","INTERSECT",VERTEX,{"derivedFrom":[subQ5,subQ0]});Q44=makeQuery(id+"F15.imprint","IMPRINT",FACE,{"disambiguationData":[TD([[makeQuery(id+"F15.imprint","IMPRINT",EDGE,{"disambiguationData":[TD([[subQ6,-1.0]])],"derivedFrom":subQ5}),-1.0]])]});}
            var Q45;
            {var subQ0=sQuery(id+"F15.wireOp",EDGE,"E15.5.1");var subQ1=sQuery(id+"F15.wireOp",EDGE,"E15.2.0");var subQ2=makeQuery(id+"F15.imprint","INTERSECT",VERTEX,{"derivedFrom":[subQ1,subQ0]});Q45=makeQuery(id+"F15.imprint","IMPRINT",FACE,{"disambiguationData":[TD([[makeQuery(id+"F15.imprint","IMPRINT",EDGE,{"disambiguationData":[TD([[subQ2,-1.0]])],"derivedFrom":subQ1}),1.0]])]});}
            var Q46;
            {var subQ0=sQuery(id+"F15.wireOp",EDGE,"E15.6.1");var subQ1=sQuery(id+"F15.wireOp",EDGE,"E15.2.0");var subQ2=makeQuery(id+"F15.imprint","INTERSECT",VERTEX,{"derivedFrom":[subQ1,subQ0]});Q46=makeQuery(id+"F15.imprint","IMPRINT",FACE,{"disambiguationData":[TD([[makeQuery(id+"F15.imprint","IMPRINT",EDGE,{"disambiguationData":[TD([[subQ2,-1.0]])],"derivedFrom":subQ1}),1.0]])]});}
            var Q47;
            {var subQ0=sQuery(id+"F15.wireOp",EDGE,"E15.9.1");var subQ1=sQuery(id+"F15.wireOp",EDGE,"E15.6.0");var subQ2=makeQuery(id+"F15.imprint","INTERSECT",VERTEX,{"derivedFrom":[subQ1,subQ0]});Q47=makeQuery(id+"F15.imprint","IMPRINT",FACE,{"disambiguationData":[TD([[makeQuery(id+"F15.imprint","IMPRINT",EDGE,{"disambiguationData":[TD([[subQ2,-1.0]])],"derivedFrom":subQ1}),1.0]])]});}
            var Q48;
            {var subQ0=sQuery(id+"F15.wireOp",EDGE,"E15.7.1");var subQ5=sQuery(id+"F15.wireOp",EDGE,"E15.3.0");var subQ7=makeQuery(id+"F15.imprint","INTERSECT",VERTEX,{"derivedFrom":[subQ5,subQ0]});Q48=makeQuery(id+"F15.imprint","IMPRINT",FACE,{"disambiguationData":[TD([[makeQuery(id+"F15.imprint","IMPRINT",EDGE,{"disambiguationData":[TD([[subQ7,-1.0]])],"derivedFrom":subQ5}),-1.0]])]});}
            var Q49;
            {var subQ0=sQuery(id+"F15.wireOp",EDGE,"E15.8.0");var subQ1=sQuery(id+"F15.wireOp",EDGE,"E15.1.1");var subQ2=makeQuery(id+"F15.imprint","INTERSECT",VERTEX,{"derivedFrom":[subQ1,subQ0]});Q49=makeQuery(id+"F15.imprint","IMPRINT",FACE,{"disambiguationData":[TD([[makeQuery(id+"F15.imprint","IMPRINT",EDGE,{"disambiguationData":[TD([[subQ2,-1.0]])],"derivedFrom":subQ1}),1.0]])]});}
            var Q50;
            {var subQ1=sQuery(id+"F15.wireOp",EDGE,"E15.2.0");var subQ3=sQuery(id+"F15.wireOp",EDGE,"E15.6.1");var subQ4=makeQuery(id+"F15.imprint","INTERSECT",VERTEX,{"derivedFrom":[subQ1,subQ3]});Q50=makeQuery(id+"F15.imprint","IMPRINT",FACE,{"disambiguationData":[TD([[makeQuery(id+"F15.imprint","IMPRINT",EDGE,{"disambiguationData":[TD([[subQ4,1.0]])],"derivedFrom":subQ1}),-1.0]])]});}
            var Q51;
            {var subQ1=sQuery(id+"F15.wireOp",EDGE,"E15.2.1");var subQ3=sQuery(id+"F15.wireOp",EDGE,"E15.8.0");var subQ4=makeQuery(id+"F15.imprint","INTERSECT",VERTEX,{"derivedFrom":[subQ1,subQ3]});Q51=makeQuery(id+"F15.imprint","IMPRINT",FACE,{"disambiguationData":[TD([[makeQuery(id+"F15.imprint","IMPRINT",EDGE,{"disambiguationData":[TD([[subQ4,1.0]])],"derivedFrom":subQ1}),1.0]])]});}
            var Q52;
            {var subQ1=sQuery(id+"F15.wireOp",EDGE,"E14.right");var subQ3=sQuery(id+"F15.wireOp",EDGE,"E15.6.0");var subQ4=makeQuery(id+"F15.imprint","INTERSECT",VERTEX,{"derivedFrom":[subQ1,subQ3]});Q52=makeQuery(id+"F15.imprint","IMPRINT",FACE,{"disambiguationData":[TD([[makeQuery(id+"F15.imprint","IMPRINT",EDGE,{"disambiguationData":[TD([[subQ4,1.0]])],"derivedFrom":subQ1}),1.0]])]});}
            var Q53;
            {var subQ0=sQuery(id+"F15.wireOp",EDGE,"E15.5.1");var subQ1=sQuery(id+"F15.wireOp",EDGE,"E15.1.0");var subQ2=makeQuery(id+"F15.imprint","INTERSECT",VERTEX,{"derivedFrom":[subQ1,subQ0]});Q53=makeQuery(id+"F15.imprint","IMPRINT",FACE,{"disambiguationData":[TD([[makeQuery(id+"F15.imprint","IMPRINT",EDGE,{"disambiguationData":[TD([[subQ2,-1.0]])],"derivedFrom":subQ1}),1.0]])]});}
            var Q54;
            {var subQ0=sQuery(id+"F15.wireOp",EDGE,"E15.3.1");var subQ1=sQuery(id+"F15.wireOp",EDGE,"E14.left");var subQ2=makeQuery(id+"F15.imprint","INTERSECT",VERTEX,{"derivedFrom":[subQ1,subQ0]});Q54=makeQuery(id+"F15.imprint","IMPRINT",FACE,{"disambiguationData":[TD([[makeQuery(id+"F15.imprint","IMPRINT",EDGE,{"disambiguationData":[TD([[subQ2,-1.0]])],"derivedFrom":subQ1}),1.0]])]});}
            var Q55;
            {var subQ0=sQuery(id+"F15.wireOp",EDGE,"E15.3.1");var subQ1=sQuery(id+"F15.wireOp",EDGE,"E14.left");var subQ2=makeQuery(id+"F15.imprint","INTERSECT",VERTEX,{"derivedFrom":[subQ1,subQ0]});Q55=makeQuery(id+"F15.imprint","IMPRINT",FACE,{"disambiguationData":[TD([[makeQuery(id+"F15.imprint","IMPRINT",EDGE,{"disambiguationData":[TD([[subQ2,-1.0]])],"derivedFrom":subQ1}),-1.0]])]});}
            var Q56;
            {var subQ0=sQuery(id+"F15.wireOp",EDGE,"E15.9.1");var subQ5=sQuery(id+"F15.wireOp",EDGE,"E15.5.0");var subQ6=makeQuery(id+"F15.imprint","INTERSECT",VERTEX,{"derivedFrom":[subQ5,subQ0]});Q56=makeQuery(id+"F15.imprint","IMPRINT",FACE,{"disambiguationData":[TD([[makeQuery(id+"F15.imprint","IMPRINT",EDGE,{"disambiguationData":[TD([[subQ6,-1.0]])],"derivedFrom":subQ5}),-1.0]])]});}
            var Q57;
            {var subQ1=sQuery(id+"F15.wireOp",EDGE,"E15.3.1");var subQ3=sQuery(id+"F15.wireOp",EDGE,"E15.9.0");var subQ4=makeQuery(id+"F15.imprint","INTERSECT",VERTEX,{"derivedFrom":[subQ1,subQ3]});Q57=makeQuery(id+"F15.imprint","IMPRINT",FACE,{"disambiguationData":[TD([[makeQuery(id+"F15.imprint","IMPRINT",EDGE,{"disambiguationData":[TD([[subQ4,1.0]])],"derivedFrom":subQ1}),1.0]])]});}
            var Q58;
            {var subQ0=sQuery(id+"F15.wireOp",EDGE,"E15.7.0");var subQ1=sQuery(id+"F15.wireOp",EDGE,"E14.right");var subQ2=makeQuery(id+"F15.imprint","INTERSECT",VERTEX,{"derivedFrom":[subQ1,subQ0]});Q58=makeQuery(id+"F15.imprint","IMPRINT",FACE,{"disambiguationData":[TD([[makeQuery(id+"F15.imprint","IMPRINT",EDGE,{"disambiguationData":[TD([[subQ2,-1.0]])],"derivedFrom":subQ1}),1.0]])]});}
            var Q59;
            {var subQ0=sQuery(id+"F15.wireOp",EDGE,"E15.6.0");var subQ1=sQuery(id+"F15.wireOp",EDGE,"E14.right");var subQ2=makeQuery(id+"F15.imprint","INTERSECT",VERTEX,{"derivedFrom":[subQ1,subQ0]});Q59=makeQuery(id+"F15.imprint","IMPRINT",FACE,{"disambiguationData":[TD([[makeQuery(id+"F15.imprint","IMPRINT",EDGE,{"disambiguationData":[TD([[subQ2,-1.0]])],"derivedFrom":subQ1}),1.0]])]});}
            var Q60;
            {var subQ0=sQuery(id+"F15.wireOp",EDGE,"E15.8.0");var subQ1=sQuery(id+"F15.wireOp",EDGE,"E15.2.1");var subQ2=makeQuery(id+"F15.imprint","INTERSECT",VERTEX,{"derivedFrom":[subQ1,subQ0]});Q60=makeQuery(id+"F15.imprint","IMPRINT",FACE,{"disambiguationData":[TD([[makeQuery(id+"F15.imprint","IMPRINT",EDGE,{"disambiguationData":[TD([[subQ2,-1.0]])],"derivedFrom":subQ1}),1.0]])]});}
            var Q61;
            {var subQ0=sQuery(id+"F15.wireOp",EDGE,"E15.8.1");var subQ5=sQuery(id+"F15.wireOp",EDGE,"E15.4.0");var subQ6=makeQuery(id+"F15.imprint","INTERSECT",VERTEX,{"derivedFrom":[subQ5,subQ0]});Q61=makeQuery(id+"F15.imprint","IMPRINT",FACE,{"disambiguationData":[TD([[makeQuery(id+"F15.imprint","IMPRINT",EDGE,{"disambiguationData":[TD([[subQ6,-1.0]])],"derivedFrom":subQ5}),-1.0]])]});}
            var Q62;
            {var subQ0=sQuery(id+"F15.wireOp",EDGE,"E15.4.1");var subQ1=sQuery(id+"F15.wireOp",EDGE,"E15.1.0");var subQ2=makeQuery(id+"F15.imprint","INTERSECT",VERTEX,{"derivedFrom":[subQ1,subQ0]});Q62=makeQuery(id+"F15.imprint","IMPRINT",FACE,{"disambiguationData":[TD([[makeQuery(id+"F15.imprint","IMPRINT",EDGE,{"disambiguationData":[TD([[subQ2,-1.0]])],"derivedFrom":subQ1}),1.0]])]});}
            extrude(context, id + "F16", {"entities" : qUnion([Q0, Q1, Q2, Q3, Q4, Q5, Q6, Q7, Q8, Q9, Q10, Q11, Q12, Q13, Q14, Q15, Q16, Q17, Q18, Q19, Q20, Q21, Q22, Q23, Q24, Q25, Q26, Q27, Q28, Q29, Q30, Q31, Q32, Q33, Q34, Q35, Q36, Q37, Q38, Q39, Q40, Q41, Q42, Q43, Q44, Q45, Q46, Q47, Q48, Q49, Q50, Q51, Q52, Q53, Q54, Q55, Q56, Q57, Q58, Q59, Q60, Q61, Q62]), "operationType" : NewBodyOperationType.REMOVE, "oppositeDirection" : true, "depth" : 10 * mm, "offsetDistance" : 25 * mm});
        }
        {
            var Q0;
            Q0=makeQuery(id+"F4.opLoft","SWEPT_FACE",FACE,{"disambiguationData":[OSD([sQuery(id+"F0.wireOp",EDGE,"E0.bottom"),sQuery(id+"F0.wireOp",EDGE,"E0.top"),sQuery(id+"F0.wireOp",EDGE,"E0.right"),sQuery(id+"F3.wireOp",EDGE,"E1.bottom"),sQuery(id+"F3.wireOp",EDGE,"E1.top"),sQuery(id+"F3.wireOp",EDGE,"E1.right")])]});
            var sketch = newSketch(context, id + "F17", { "sketchPlane" : qUnion([Q0])});
            skPoint(sketch, "E16", {"position": v(0, 82.05) * mm});
            skPoint(sketch, "E16.positionSnap0", {"position": v(0, 117.05) * mm});
            skLineSegment(sketch, "E17.bottom", {"start": v(25, 57.05) * mm, "end": v(-25, 57.05) * mm});
            skLineSegment(sketch, "E17.top", {"start": v(25, 107.05) * mm, "end": v(-25, 107.05) * mm});
            skLineSegment(sketch, "E17.left", {"start": v(25, 57.05) * mm, "end": v(25, 107.05) * mm});
            skLineSegment(sketch, "E17.right", {"start": v(-25, 57.05) * mm, "end": v(-25, 107.05) * mm});
            skSolve(sketch);
        }
        {
            var Q0;
            Q0=makeQuery(id+"F17.imprint","IMPRINT",FACE,{"disambiguationData":[TD([[makeQuery(id+"F17.imprint","IMPRINT",EDGE,{"derivedFrom":sQuery(id+"F17.wireOp",EDGE,"E17.bottom")}),-1.0]])]});
            extrude(context, id + "F18", {"entities" : qUnion([Q0]), "operationType" : NewBodyOperationType.REMOVE, "oppositeDirection" : true, "depth" : 10 * mm, "offsetDistance" : 25 * mm});
        }
        {
            var Q0;
            Q0=makeQuery(id+"F18.boolean.opBoolean","COPY",FACE,{"derivedFrom":makeQuery(id+"F18.opExtrude","CAP_FACE",FACE,{"disambiguationData":[OSD([sQuery(id+"F17.wireOp",EDGE,"E17.bottom"),sQuery(id+"F17.wireOp",EDGE,"E17.top"),sQuery(id+"F17.wireOp",EDGE,"E17.left"),sQuery(id+"F17.wireOp",EDGE,"E17.right")])],"isStart":false})});
            var sketch = newSketch(context, id + "F19", { "sketchPlane" : qUnion([Q0])});
            skLineSegment(sketch, "E18.bottom", {"start": v(20, 62.05) * mm, "end": v(-20, 62.05) * mm});
            skLineSegment(sketch, "E18.top", {"start": v(20, 102.05) * mm, "end": v(-20, 102.05) * mm});
            skLineSegment(sketch, "E18.left", {"start": v(20, 62.05) * mm, "end": v(20, 102.05) * mm});
            skLineSegment(sketch, "E18.right", {"start": v(-20, 62.05) * mm, "end": v(-20, 102.05) * mm});
            skPoint(sketch, "E18.middle", {"position": v(0, 82.05) * mm});
            skPoint(sketch, "E18.middle.positionSnap0", {"position": v(25, 82.05) * mm});
            skPoint(sketch, "E18.middle.positionSnap1", {"position": v(0, 107.05) * mm});
            skPoint(sketch, "E18.centerSnap0", {"position": v(25, 82.05) * mm});
            skPoint(sketch, "E18.centerSnap1", {"position": v(0, 107.05) * mm});
            skSolve(sketch);
        }
        {
            var Q0;
            Q0=makeQuery(id+"F19.imprint","IMPRINT",FACE,{"disambiguationData":[TD([[makeQuery(id+"F19.imprint","IMPRINT",EDGE,{"derivedFrom":sQuery(id+"F19.wireOp",EDGE,"E18.bottom")}),-1.0]])]});
            extrude(context, id + "F20", {"entities" : qUnion([Q0]), "operationType" : NewBodyOperationType.REMOVE, "oppositeDirection" : true, "depth" : 25 * mm, "offsetDistance" : 25 * mm});
        }
        {
            var Q0;
            Q0=makeQuery(id+"F18.boolean.opBoolean","COPY",FACE,{"derivedFrom":makeQuery(id+"F18.opExtrude","CAP_FACE",FACE,{"disambiguationData":[OSD([sQuery(id+"F17.wireOp",EDGE,"E17.bottom"),sQuery(id+"F17.wireOp",EDGE,"E17.top"),sQuery(id+"F17.wireOp",EDGE,"E17.left"),sQuery(id+"F17.wireOp",EDGE,"E17.right")])],"isStart":false})});
            var sketch = newSketch(context, id + "F21", { "sketchPlane" : qUnion([Q0])});
            skLineSegment(sketch, "E19.bottom", {"start": v(25, 57.05) * mm, "end": v(-25, 57.05) * mm});
            skLineSegment(sketch, "E19.top", {"start": v(25, 107.05) * mm, "end": v(-25, 107.05) * mm});
            skLineSegment(sketch, "E19.left", {"start": v(25, 57.05) * mm, "end": v(25, 107.05) * mm});
            skLineSegment(sketch, "E19.right", {"start": v(-25, 57.05) * mm, "end": v(-25, 107.05) * mm});
            skPoint(sketch, "E19.middle", {"position": v(0, 82.05) * mm});
            skPoint(sketch, "E19.middle.positionSnap0", {"position": v(20, 82.05) * mm});
            skPoint(sketch, "E19.middle.positionSnap1", {"position": v(0, 102.05) * mm});
            skPoint(sketch, "E19.centerSnap0", {"position": v(20, 82.05) * mm});
            skPoint(sketch, "E19.centerSnap1", {"position": v(0, 102.05) * mm});
            skSolve(sketch);
        }
        {
            var Q0;
            Q0=makeQuery(id+"F21.imprint","IMPRINT",FACE,{"disambiguationData":[TD([[makeQuery(id+"F21.imprint","IMPRINT",EDGE,{"derivedFrom":sQuery(id+"F21.wireOp",EDGE,"E19.bottom")}),-1.0]])]});
            var Q1;
            Q1=makeQuery(id+"F21.imprint","IMPRINT",FACE,{"disambiguationData":[TD([[makeQuery(id+"F21.imprint","IMPRINT",EDGE,{"derivedFrom":makeQuery(id+"F20.boolean.opBoolean","COPY",EDGE,{"derivedFrom":makeQuery(id+"F20.opExtrude","CAP_EDGE",EDGE,{"disambiguationData":[OSD([sQuery(id+"F19.wireOp",EDGE,"E18.bottom")])],"isStart":true})})}),-1.0]])]});
            extrude(context, id + "F22", {"entities" : qUnion([Q0, Q1]), "operationType" : NewBodyOperationType.ADD, "depth" : 10 * mm, "offsetDistance" : 25 * mm});
        }
        {
            var Q0;
            Q0=makeQuery(id+"F22.boolean.opBoolean","MERGE",FACE,{"derivedFrom":[makeQuery(id+"F4.opLoft","SWEPT_FACE",FACE,{"disambiguationData":[OSD([sQuery(id+"F0.wireOp",EDGE,"E0.bottom"),sQuery(id+"F0.wireOp",EDGE,"E0.top"),sQuery(id+"F0.wireOp",EDGE,"E0.right"),sQuery(id+"F3.wireOp",EDGE,"E1.bottom"),sQuery(id+"F3.wireOp",EDGE,"E1.top"),sQuery(id+"F3.wireOp",EDGE,"E1.right")])]}),makeQuery(id+"F22.opExtrude","CAP_FACE",FACE,{"disambiguationData":[OSD([sQuery(id+"F21.wireOp",EDGE,"E19.bottom"),sQuery(id+"F21.wireOp",EDGE,"E19.top"),sQuery(id+"F21.wireOp",EDGE,"E19.left"),sQuery(id+"F21.wireOp",EDGE,"E19.right")])],"isStart":false})]});
            var sketch = newSketch(context, id + "F23", { "sketchPlane" : qUnion([Q0])});
            skPoint(sketch, "E20", {"position": v(0, 82.05) * mm});
            skPoint(sketch, "E20.positionSnap0", {"position": v(0, 117.05) * mm});
            skCircle(sketch, "E21", {"center": v(0, 82.05) * mm, "radius": 17.5 * mm});
            skCircle(sketch, "E22", {"center": v(0, 82.05) * mm, "radius": 12.5 * mm});
            skLineSegment(sketch, "E23.bottom", {"start": v(-2.5, 82.05) * mm, "end": v(2.5, 82.05) * mm});
            skLineSegment(sketch, "E23.top", {"start": v(-2.5, 102.87) * mm, "end": v(2.5, 102.87) * mm});
            skLineSegment(sketch, "E23.left", {"start": v(-2.5, 82.05) * mm, "end": v(-2.5, 102.87) * mm});
            skLineSegment(sketch, "E23.right", {"start": v(2.5, 82.05) * mm, "end": v(2.5, 102.87) * mm});
            skLineSegment(sketch, "E24.1.0", {"start": v(-2.02, 80.58) * mm, "end": v(-14.26, 97.42) * mm});
            skLineSegment(sketch, "E24.1.1", {"start": v(2.02, 83.52) * mm, "end": v(-10.21, 100.36) * mm});
            skLineSegment(sketch, "E24.1.2", {"start": v(-14.26, 97.42) * mm, "end": v(-10.21, 100.36) * mm});
            skLineSegment(sketch, "E24.1.3", {"start": v(-2.02, 80.58) * mm, "end": v(2.02, 83.52) * mm});
            skLineSegment(sketch, "E24.2.0", {"start": v(-0.77, 79.68) * mm, "end": v(-20.57, 86.1) * mm});
            skLineSegment(sketch, "E24.2.1", {"start": v(0.77, 84.43) * mm, "end": v(-19.02, 90.86) * mm});
            skLineSegment(sketch, "E24.2.2", {"start": v(-20.57, 86.1) * mm, "end": v(-19.02, 90.86) * mm});
            skLineSegment(sketch, "E24.2.3", {"start": v(-0.77, 79.68) * mm, "end": v(0.77, 84.43) * mm});
            skLineSegment(sketch, "E24.3.0", {"start": v(0.77, 79.68) * mm, "end": v(-19.02, 73.25) * mm});
            skLineSegment(sketch, "E24.3.1", {"start": v(-0.77, 84.43) * mm, "end": v(-20.57, 78) * mm});
            skLineSegment(sketch, "E24.3.2", {"start": v(-19.02, 73.25) * mm, "end": v(-20.57, 78) * mm});
            skLineSegment(sketch, "E24.3.3", {"start": v(0.77, 79.68) * mm, "end": v(-0.77, 84.43) * mm});
            skLineSegment(sketch, "E24.4.0", {"start": v(2.02, 80.58) * mm, "end": v(-10.21, 63.75) * mm});
            skLineSegment(sketch, "E24.4.1", {"start": v(-2.02, 83.52) * mm, "end": v(-14.26, 66.69) * mm});
            skLineSegment(sketch, "E24.4.2", {"start": v(-10.21, 63.75) * mm, "end": v(-14.26, 66.69) * mm});
            skLineSegment(sketch, "E24.4.3", {"start": v(2.02, 80.58) * mm, "end": v(-2.02, 83.52) * mm});
            skLineSegment(sketch, "E24.5.0", {"start": v(2.5, 82.05) * mm, "end": v(2.5, 61.24) * mm});
            skLineSegment(sketch, "E24.5.1", {"start": v(-2.5, 82.05) * mm, "end": v(-2.5, 61.24) * mm});
            skLineSegment(sketch, "E24.5.2", {"start": v(2.5, 61.24) * mm, "end": v(-2.5, 61.24) * mm});
            skLineSegment(sketch, "E24.5.3", {"start": v(2.5, 82.05) * mm, "end": v(-2.5, 82.05) * mm});
            skLineSegment(sketch, "E24.6.0", {"start": v(2.02, 83.52) * mm, "end": v(14.26, 66.69) * mm});
            skLineSegment(sketch, "E24.6.1", {"start": v(-2.02, 80.58) * mm, "end": v(10.21, 63.75) * mm});
            skLineSegment(sketch, "E24.6.2", {"start": v(14.26, 66.69) * mm, "end": v(10.21, 63.75) * mm});
            skLineSegment(sketch, "E24.6.3", {"start": v(2.02, 83.52) * mm, "end": v(-2.02, 80.58) * mm});
            skLineSegment(sketch, "E24.7.0", {"start": v(0.77, 84.43) * mm, "end": v(20.57, 78) * mm});
            skLineSegment(sketch, "E24.7.1", {"start": v(-0.77, 79.68) * mm, "end": v(19.02, 73.25) * mm});
            skLineSegment(sketch, "E24.7.2", {"start": v(20.57, 78) * mm, "end": v(19.02, 73.25) * mm});
            skLineSegment(sketch, "E24.7.3", {"start": v(0.77, 84.43) * mm, "end": v(-0.77, 79.68) * mm});
            skLineSegment(sketch, "E24.8.0", {"start": v(-0.77, 84.43) * mm, "end": v(19.02, 90.86) * mm});
            skLineSegment(sketch, "E24.8.1", {"start": v(0.77, 79.68) * mm, "end": v(20.57, 86.1) * mm});
            skLineSegment(sketch, "E24.8.2", {"start": v(19.02, 90.86) * mm, "end": v(20.57, 86.1) * mm});
            skLineSegment(sketch, "E24.8.3", {"start": v(-0.77, 84.43) * mm, "end": v(0.77, 79.68) * mm});
            skLineSegment(sketch, "E24.9.0", {"start": v(-2.02, 83.52) * mm, "end": v(10.21, 100.36) * mm});
            skLineSegment(sketch, "E24.9.1", {"start": v(2.02, 80.58) * mm, "end": v(14.26, 97.42) * mm});
            skLineSegment(sketch, "E24.9.2", {"start": v(10.21, 100.36) * mm, "end": v(14.26, 97.42) * mm});
            skLineSegment(sketch, "E24.9.3", {"start": v(-2.02, 83.52) * mm, "end": v(2.02, 80.58) * mm});
            skSolve(sketch);
        }
        {
            var Q0;
            {var subQ0=sQuery(id+"F23.wireOp",EDGE,"E23.right");var subQ1=sQuery(id+"F23.wireOp",EDGE,"E21");var subQ2=makeQuery(id+"F23.imprint","INTERSECT",VERTEX,{"derivedFrom":[subQ1,subQ0]});Q0=makeQuery(id+"F23.imprint","IMPRINT",FACE,{"disambiguationData":[TD([[makeQuery(id+"F23.imprint","IMPRINT",EDGE,{"disambiguationData":[TD([[subQ2,-1.0]])],"derivedFrom":subQ1}),1.0]])]});}
            var Q1;
            {var subQ0=sQuery(id+"F23.wireOp",EDGE,"E23.right");var subQ1=sQuery(id+"F23.wireOp",EDGE,"E22");var subQ2=makeQuery(id+"F23.imprint","INTERSECT",VERTEX,{"derivedFrom":[subQ1,subQ0]});Q1=makeQuery(id+"F23.imprint","IMPRINT",FACE,{"disambiguationData":[TD([[makeQuery(id+"F23.imprint","IMPRINT",EDGE,{"disambiguationData":[TD([[subQ2,-1.0]])],"derivedFrom":subQ1}),1.0]])]});}
            var Q2;
            {var subQ0=sQuery(id+"F23.wireOp",EDGE,"E24.4.1");var subQ1=sQuery(id+"F23.wireOp",EDGE,"E21");var subQ2=makeQuery(id+"F23.imprint","INTERSECT",VERTEX,{"derivedFrom":[subQ1,subQ0]});Q2=makeQuery(id+"F23.imprint","IMPRINT",FACE,{"disambiguationData":[TD([[makeQuery(id+"F23.imprint","IMPRINT",EDGE,{"disambiguationData":[TD([[subQ2,-1.0]])],"derivedFrom":subQ1}),1.0]])]});}
            var Q3;
            {var subQ0=sQuery(id+"F23.wireOp",EDGE,"E24.6.1");var subQ1=sQuery(id+"F23.wireOp",EDGE,"E21");var subQ2=makeQuery(id+"F23.imprint","INTERSECT",VERTEX,{"derivedFrom":[subQ1,subQ0]});Q3=makeQuery(id+"F23.imprint","IMPRINT",FACE,{"disambiguationData":[TD([[makeQuery(id+"F23.imprint","IMPRINT",EDGE,{"disambiguationData":[TD([[subQ2,-1.0]])],"derivedFrom":subQ1}),1.0]])]});}
            var Q4;
            {var subQ0=sQuery(id+"F23.wireOp",EDGE,"E24.4.1");var subQ1=sQuery(id+"F23.wireOp",EDGE,"E22");var subQ2=makeQuery(id+"F23.imprint","INTERSECT",VERTEX,{"derivedFrom":[subQ1,subQ0]});Q4=makeQuery(id+"F23.imprint","IMPRINT",FACE,{"disambiguationData":[TD([[makeQuery(id+"F23.imprint","IMPRINT",EDGE,{"disambiguationData":[TD([[subQ2,-1.0]])],"derivedFrom":subQ1}),1.0]])]});}
            var Q5;
            {var subQ0=sQuery(id+"F23.wireOp",EDGE,"E24.6.1");var subQ1=sQuery(id+"F23.wireOp",EDGE,"E22");var subQ2=makeQuery(id+"F23.imprint","INTERSECT",VERTEX,{"derivedFrom":[subQ1,subQ0]});Q5=makeQuery(id+"F23.imprint","IMPRINT",FACE,{"disambiguationData":[TD([[makeQuery(id+"F23.imprint","IMPRINT",EDGE,{"disambiguationData":[TD([[subQ2,-1.0]])],"derivedFrom":subQ1}),1.0]])]});}
            var Q6;
            {var subQ0=sQuery(id+"F23.wireOp",EDGE,"E24.5.0");var subQ1=sQuery(id+"F23.wireOp",EDGE,"E22");var subQ2=makeQuery(id+"F23.imprint","INTERSECT",VERTEX,{"derivedFrom":[subQ1,subQ0]});Q6=makeQuery(id+"F23.imprint","IMPRINT",FACE,{"disambiguationData":[TD([[makeQuery(id+"F23.imprint","IMPRINT",EDGE,{"disambiguationData":[TD([[subQ2,-1.0]])],"derivedFrom":subQ1}),1.0]])]});}
            var Q7;
            {var subQ0=sQuery(id+"F23.wireOp",EDGE,"E24.4.0");var subQ1=sQuery(id+"F23.wireOp",EDGE,"E22");var subQ2=makeQuery(id+"F23.imprint","INTERSECT",VERTEX,{"derivedFrom":[subQ1,subQ0]});Q7=makeQuery(id+"F23.imprint","IMPRINT",FACE,{"disambiguationData":[TD([[makeQuery(id+"F23.imprint","IMPRINT",EDGE,{"disambiguationData":[TD([[subQ2,-1.0]])],"derivedFrom":subQ1}),1.0]])]});}
            var Q8;
            {var subQ0=sQuery(id+"F23.wireOp",EDGE,"E24.5.1");var subQ1=sQuery(id+"F23.wireOp",EDGE,"E22");var subQ2=makeQuery(id+"F23.imprint","INTERSECT",VERTEX,{"derivedFrom":[subQ1,subQ0]});Q8=makeQuery(id+"F23.imprint","IMPRINT",FACE,{"disambiguationData":[TD([[makeQuery(id+"F23.imprint","IMPRINT",EDGE,{"disambiguationData":[TD([[subQ2,-1.0]])],"derivedFrom":subQ1}),1.0]])]});}
            var Q9;
            {var subQ0=sQuery(id+"F23.wireOp",EDGE,"E24.3.0");var subQ1=sQuery(id+"F23.wireOp",EDGE,"E22");var subQ2=makeQuery(id+"F23.imprint","INTERSECT",VERTEX,{"derivedFrom":[subQ1,subQ0]});Q9=makeQuery(id+"F23.imprint","IMPRINT",FACE,{"disambiguationData":[TD([[makeQuery(id+"F23.imprint","IMPRINT",EDGE,{"disambiguationData":[TD([[subQ2,-1.0]])],"derivedFrom":subQ1}),1.0]])]});}
            var Q10;
            {var subQ0=sQuery(id+"F23.wireOp",EDGE,"E24.2.0");var subQ1=sQuery(id+"F23.wireOp",EDGE,"E22");var subQ2=makeQuery(id+"F23.imprint","INTERSECT",VERTEX,{"derivedFrom":[subQ1,subQ0]});Q10=makeQuery(id+"F23.imprint","IMPRINT",FACE,{"disambiguationData":[TD([[makeQuery(id+"F23.imprint","IMPRINT",EDGE,{"disambiguationData":[TD([[subQ2,-1.0]])],"derivedFrom":subQ1}),1.0]])]});}
            var Q11;
            {var subQ0=sQuery(id+"F23.wireOp",EDGE,"E24.3.1");var subQ1=sQuery(id+"F23.wireOp",EDGE,"E22");var subQ2=makeQuery(id+"F23.imprint","INTERSECT",VERTEX,{"derivedFrom":[subQ1,subQ0]});Q11=makeQuery(id+"F23.imprint","IMPRINT",FACE,{"disambiguationData":[TD([[makeQuery(id+"F23.imprint","IMPRINT",EDGE,{"disambiguationData":[TD([[subQ2,-1.0]])],"derivedFrom":subQ1}),1.0]])]});}
            var Q12;
            {var subQ0=sQuery(id+"F23.wireOp",EDGE,"E24.1.0");var subQ1=sQuery(id+"F23.wireOp",EDGE,"E22");var subQ2=makeQuery(id+"F23.imprint","INTERSECT",VERTEX,{"derivedFrom":[subQ1,subQ0]});Q12=makeQuery(id+"F23.imprint","IMPRINT",FACE,{"disambiguationData":[TD([[makeQuery(id+"F23.imprint","IMPRINT",EDGE,{"disambiguationData":[TD([[subQ2,-1.0]])],"derivedFrom":subQ1}),1.0]])]});}
            var Q13;
            {var subQ0=sQuery(id+"F23.wireOp",EDGE,"E24.2.1");var subQ1=sQuery(id+"F23.wireOp",EDGE,"E22");var subQ2=makeQuery(id+"F23.imprint","INTERSECT",VERTEX,{"derivedFrom":[subQ1,subQ0]});Q13=makeQuery(id+"F23.imprint","IMPRINT",FACE,{"disambiguationData":[TD([[makeQuery(id+"F23.imprint","IMPRINT",EDGE,{"disambiguationData":[TD([[subQ2,-1.0]])],"derivedFrom":subQ1}),1.0]])]});}
            var Q14;
            {var subQ1=sQuery(id+"F23.wireOp",EDGE,"E22");var subQ5=sQuery(id+"F23.wireOp",EDGE,"E24.1.1");var subQ6=makeQuery(id+"F23.imprint","INTERSECT",VERTEX,{"derivedFrom":[subQ1,subQ5]});Q14=makeQuery(id+"F23.imprint","IMPRINT",FACE,{"disambiguationData":[TD([[makeQuery(id+"F23.imprint","IMPRINT",EDGE,{"disambiguationData":[TD([[subQ6,-1.0]])],"derivedFrom":subQ1}),1.0]])]});}
            var Q15;
            {var subQ0=sQuery(id+"F23.wireOp",EDGE,"E23.left");var subQ1=sQuery(id+"F23.wireOp",EDGE,"E22");var subQ2=makeQuery(id+"F23.imprint","INTERSECT",VERTEX,{"derivedFrom":[subQ1,subQ0]});Q15=makeQuery(id+"F23.imprint","IMPRINT",FACE,{"disambiguationData":[TD([[makeQuery(id+"F23.imprint","IMPRINT",EDGE,{"disambiguationData":[TD([[subQ2,-1.0]])],"derivedFrom":subQ1}),1.0]])]});}
            var Q16;
            {var subQ3=sQuery(id+"F23.wireOp",EDGE,"E24.9.1");var subQ7=sQuery(id+"F23.wireOp",EDGE,"E22");var subQ8=makeQuery(id+"F23.imprint","INTERSECT",VERTEX,{"derivedFrom":[subQ7,subQ3]});Q16=makeQuery(id+"F23.imprint","IMPRINT",FACE,{"disambiguationData":[TD([[makeQuery(id+"F23.imprint","IMPRINT",EDGE,{"disambiguationData":[TD([[subQ8,-1.0]])],"derivedFrom":subQ7}),1.0]])]});}
            var Q17;
            {var subQ0=sQuery(id+"F23.wireOp",EDGE,"E24.9.0");var subQ1=sQuery(id+"F23.wireOp",EDGE,"E22");var subQ2=makeQuery(id+"F23.imprint","INTERSECT",VERTEX,{"derivedFrom":[subQ1,subQ0]});Q17=makeQuery(id+"F23.imprint","IMPRINT",FACE,{"disambiguationData":[TD([[makeQuery(id+"F23.imprint","IMPRINT",EDGE,{"disambiguationData":[TD([[subQ2,-1.0]])],"derivedFrom":subQ1}),1.0]])]});}
            var Q18;
            {var subQ1=sQuery(id+"F23.wireOp",EDGE,"E22");var subQ7=sQuery(id+"F23.wireOp",EDGE,"E24.8.0");var subQ8=makeQuery(id+"F23.imprint","INTERSECT",VERTEX,{"derivedFrom":[subQ1,subQ7]});Q18=makeQuery(id+"F23.imprint","IMPRINT",FACE,{"disambiguationData":[TD([[makeQuery(id+"F23.imprint","IMPRINT",EDGE,{"disambiguationData":[TD([[subQ8,1.0]])],"derivedFrom":subQ1}),1.0]])]});}
            var Q19;
            {var subQ0=sQuery(id+"F23.wireOp",EDGE,"E24.8.0");var subQ1=sQuery(id+"F23.wireOp",EDGE,"E22");var subQ2=makeQuery(id+"F23.imprint","INTERSECT",VERTEX,{"derivedFrom":[subQ1,subQ0]});Q19=makeQuery(id+"F23.imprint","IMPRINT",FACE,{"disambiguationData":[TD([[makeQuery(id+"F23.imprint","IMPRINT",EDGE,{"disambiguationData":[TD([[subQ2,-1.0]])],"derivedFrom":subQ1}),1.0]])]});}
            var Q20;
            {var subQ0=sQuery(id+"F23.wireOp",EDGE,"E24.7.1");var subQ1=sQuery(id+"F23.wireOp",EDGE,"E22");var subQ2=makeQuery(id+"F23.imprint","INTERSECT",VERTEX,{"derivedFrom":[subQ1,subQ0]});Q20=makeQuery(id+"F23.imprint","IMPRINT",FACE,{"disambiguationData":[TD([[makeQuery(id+"F23.imprint","IMPRINT",EDGE,{"disambiguationData":[TD([[subQ2,-1.0]])],"derivedFrom":subQ1}),1.0]])]});}
            var Q21;
            {var subQ0=sQuery(id+"F23.wireOp",EDGE,"E24.8.1");var subQ1=sQuery(id+"F23.wireOp",EDGE,"E22");var subQ2=makeQuery(id+"F23.imprint","INTERSECT",VERTEX,{"derivedFrom":[subQ1,subQ0]});Q21=makeQuery(id+"F23.imprint","IMPRINT",FACE,{"disambiguationData":[TD([[makeQuery(id+"F23.imprint","IMPRINT",EDGE,{"disambiguationData":[TD([[subQ2,1.0]])],"derivedFrom":subQ1}),1.0]])]});}
            var Q22;
            {var subQ0=sQuery(id+"F23.wireOp",EDGE,"E24.6.0");var subQ1=sQuery(id+"F23.wireOp",EDGE,"E22");var subQ2=makeQuery(id+"F23.imprint","INTERSECT",VERTEX,{"derivedFrom":[subQ1,subQ0]});Q22=makeQuery(id+"F23.imprint","IMPRINT",FACE,{"disambiguationData":[TD([[makeQuery(id+"F23.imprint","IMPRINT",EDGE,{"disambiguationData":[TD([[subQ2,-1.0]])],"derivedFrom":subQ1}),1.0]])]});}
            var Q23;
            {var subQ1=sQuery(id+"F23.wireOp",EDGE,"E24.2.1");var subQ3=sQuery(id+"F23.wireOp",EDGE,"E24.8.0");var subQ4=makeQuery(id+"F23.imprint","INTERSECT",VERTEX,{"derivedFrom":[subQ1,subQ3]});Q23=makeQuery(id+"F23.imprint","IMPRINT",FACE,{"disambiguationData":[TD([[makeQuery(id+"F23.imprint","IMPRINT",EDGE,{"disambiguationData":[TD([[subQ4,1.0]])],"derivedFrom":subQ1}),1.0]])]});}
            var Q24;
            {var subQ0=sQuery(id+"F23.wireOp",EDGE,"E24.7.1");var subQ1=sQuery(id+"F23.wireOp",EDGE,"E24.3.0");var subQ2=makeQuery(id+"F23.imprint","INTERSECT",VERTEX,{"derivedFrom":[subQ1,subQ0]});Q24=makeQuery(id+"F23.imprint","IMPRINT",FACE,{"disambiguationData":[TD([[makeQuery(id+"F23.imprint","IMPRINT",EDGE,{"disambiguationData":[TD([[subQ2,-1.0]])],"derivedFrom":subQ1}),1.0]])]});}
            var Q25;
            {var subQ1=sQuery(id+"F23.wireOp",EDGE,"E24.1.1");var subQ3=sQuery(id+"F23.wireOp",EDGE,"E24.7.0");var subQ4=makeQuery(id+"F23.imprint","INTERSECT",VERTEX,{"derivedFrom":[subQ1,subQ3]});Q25=makeQuery(id+"F23.imprint","IMPRINT",FACE,{"disambiguationData":[TD([[makeQuery(id+"F23.imprint","IMPRINT",EDGE,{"disambiguationData":[TD([[subQ4,1.0]])],"derivedFrom":subQ1}),1.0]])]});}
            var Q26;
            {var subQ1=sQuery(id+"F23.wireOp",EDGE,"E24.2.0");var subQ3=sQuery(id+"F23.wireOp",EDGE,"E24.6.1");var subQ4=makeQuery(id+"F23.imprint","INTERSECT",VERTEX,{"derivedFrom":[subQ1,subQ3]});Q26=makeQuery(id+"F23.imprint","IMPRINT",FACE,{"disambiguationData":[TD([[makeQuery(id+"F23.imprint","IMPRINT",EDGE,{"disambiguationData":[TD([[subQ4,1.0]])],"derivedFrom":subQ1}),-1.0]])]});}
            var Q27;
            {var subQ0=sQuery(id+"F23.wireOp",EDGE,"E24.5.1");var subQ5=sQuery(id+"F23.wireOp",EDGE,"E24.1.0");var subQ6=makeQuery(id+"F23.imprint","INTERSECT",VERTEX,{"derivedFrom":[subQ5,subQ0]});Q27=makeQuery(id+"F23.imprint","IMPRINT",FACE,{"disambiguationData":[TD([[makeQuery(id+"F23.imprint","IMPRINT",EDGE,{"disambiguationData":[TD([[subQ6,-1.0]])],"derivedFrom":subQ5}),-1.0]])]});}
            var Q28;
            {var subQ0=sQuery(id+"F23.wireOp",EDGE,"E24.8.1");var subQ1=sQuery(id+"F23.wireOp",EDGE,"E24.4.0");var subQ2=makeQuery(id+"F23.imprint","INTERSECT",VERTEX,{"derivedFrom":[subQ1,subQ0]});Q28=makeQuery(id+"F23.imprint","IMPRINT",FACE,{"disambiguationData":[TD([[makeQuery(id+"F23.imprint","IMPRINT",EDGE,{"disambiguationData":[TD([[subQ2,-1.0]])],"derivedFrom":subQ1}),1.0]])]});}
            var Q29;
            {var subQ0=sQuery(id+"F23.wireOp",EDGE,"E24.2.1");var subQ1=sQuery(id+"F23.wireOp",EDGE,"E23.left");var subQ2=makeQuery(id+"F23.imprint","INTERSECT",VERTEX,{"derivedFrom":[subQ1,subQ0]});Q29=makeQuery(id+"F23.imprint","IMPRINT",FACE,{"disambiguationData":[TD([[makeQuery(id+"F23.imprint","IMPRINT",EDGE,{"disambiguationData":[TD([[subQ2,-1.0]])],"derivedFrom":subQ1}),-1.0]])]});}
            var Q30;
            {var subQ1=sQuery(id+"F23.wireOp",EDGE,"E24.1.0");var subQ3=sQuery(id+"F23.wireOp",EDGE,"E24.5.1");var subQ4=makeQuery(id+"F23.imprint","INTERSECT",VERTEX,{"derivedFrom":[subQ1,subQ3]});Q30=makeQuery(id+"F23.imprint","IMPRINT",FACE,{"disambiguationData":[TD([[makeQuery(id+"F23.imprint","IMPRINT",EDGE,{"disambiguationData":[TD([[subQ4,1.0]])],"derivedFrom":subQ1}),-1.0]])]});}
            var Q31;
            {var subQ0=sQuery(id+"F23.wireOp",EDGE,"E24.6.1");var subQ1=sQuery(id+"F23.wireOp",EDGE,"E24.2.0");var subQ2=makeQuery(id+"F23.imprint","INTERSECT",VERTEX,{"derivedFrom":[subQ1,subQ0]});Q31=makeQuery(id+"F23.imprint","IMPRINT",FACE,{"disambiguationData":[TD([[makeQuery(id+"F23.imprint","IMPRINT",EDGE,{"disambiguationData":[TD([[subQ2,-1.0]])],"derivedFrom":subQ1}),1.0]])]});}
            var Q32;
            {var subQ0=sQuery(id+"F23.wireOp",EDGE,"E24.9.1");var subQ1=sQuery(id+"F23.wireOp",EDGE,"E24.6.0");var subQ2=makeQuery(id+"F23.imprint","INTERSECT",VERTEX,{"derivedFrom":[subQ1,subQ0]});Q32=makeQuery(id+"F23.imprint","IMPRINT",FACE,{"disambiguationData":[TD([[makeQuery(id+"F23.imprint","IMPRINT",EDGE,{"disambiguationData":[TD([[subQ2,-1.0]])],"derivedFrom":subQ1}),1.0]])]});}
            var Q33;
            {var subQ0=sQuery(id+"F23.wireOp",EDGE,"E24.8.0");var subQ1=sQuery(id+"F23.wireOp",EDGE,"E24.1.1");var subQ2=makeQuery(id+"F23.imprint","INTERSECT",VERTEX,{"derivedFrom":[subQ1,subQ0]});Q33=makeQuery(id+"F23.imprint","IMPRINT",FACE,{"disambiguationData":[TD([[makeQuery(id+"F23.imprint","IMPRINT",EDGE,{"disambiguationData":[TD([[subQ2,-1.0]])],"derivedFrom":subQ1}),1.0]])]});}
            var Q34;
            {var subQ0=sQuery(id+"F23.wireOp",EDGE,"E24.6.1");var subQ5=sQuery(id+"F23.wireOp",EDGE,"E24.2.0");var subQ6=makeQuery(id+"F23.imprint","INTERSECT",VERTEX,{"derivedFrom":[subQ5,subQ0]});Q34=makeQuery(id+"F23.imprint","IMPRINT",FACE,{"disambiguationData":[TD([[makeQuery(id+"F23.imprint","IMPRINT",EDGE,{"disambiguationData":[TD([[subQ6,-1.0]])],"derivedFrom":subQ5}),-1.0]])]});}
            var Q35;
            {var subQ0=sQuery(id+"F23.wireOp",EDGE,"E24.3.1");var subQ1=sQuery(id+"F23.wireOp",EDGE,"E23.left");var subQ2=makeQuery(id+"F23.imprint","INTERSECT",VERTEX,{"derivedFrom":[subQ1,subQ0]});Q35=makeQuery(id+"F23.imprint","IMPRINT",FACE,{"disambiguationData":[TD([[makeQuery(id+"F23.imprint","IMPRINT",EDGE,{"disambiguationData":[TD([[subQ2,-1.0]])],"derivedFrom":subQ1}),1.0]])]});}
            var Q36;
            {var subQ0=sQuery(id+"F23.wireOp",EDGE,"E24.5.1");var subQ1=sQuery(id+"F23.wireOp",EDGE,"E24.2.0");var subQ2=makeQuery(id+"F23.imprint","INTERSECT",VERTEX,{"derivedFrom":[subQ1,subQ0]});Q36=makeQuery(id+"F23.imprint","IMPRINT",FACE,{"disambiguationData":[TD([[makeQuery(id+"F23.imprint","IMPRINT",EDGE,{"disambiguationData":[TD([[subQ2,-1.0]])],"derivedFrom":subQ1}),1.0]])]});}
            var Q37;
            {var subQ0=sQuery(id+"F23.wireOp",EDGE,"E24.7.0");var subQ1=sQuery(id+"F23.wireOp",EDGE,"E23.right");var subQ2=makeQuery(id+"F23.imprint","INTERSECT",VERTEX,{"derivedFrom":[subQ1,subQ0]});Q37=makeQuery(id+"F23.imprint","IMPRINT",FACE,{"disambiguationData":[TD([[makeQuery(id+"F23.imprint","IMPRINT",EDGE,{"disambiguationData":[TD([[subQ2,-1.0]])],"derivedFrom":subQ1}),1.0]])]});}
            var Q38;
            {var subQ1=sQuery(id+"F23.wireOp",EDGE,"E23.right");var subQ3=sQuery(id+"F23.wireOp",EDGE,"E24.6.0");var subQ4=makeQuery(id+"F23.imprint","INTERSECT",VERTEX,{"derivedFrom":[subQ1,subQ3]});Q38=makeQuery(id+"F23.imprint","IMPRINT",FACE,{"disambiguationData":[TD([[makeQuery(id+"F23.imprint","IMPRINT",EDGE,{"disambiguationData":[TD([[subQ4,1.0]])],"derivedFrom":subQ1}),1.0]])]});}
            var Q39;
            {var subQ0=sQuery(id+"F23.wireOp",EDGE,"E24.6.1");var subQ1=sQuery(id+"F23.wireOp",EDGE,"E24.3.0");var subQ2=makeQuery(id+"F23.imprint","INTERSECT",VERTEX,{"derivedFrom":[subQ1,subQ0]});Q39=makeQuery(id+"F23.imprint","IMPRINT",FACE,{"disambiguationData":[TD([[makeQuery(id+"F23.imprint","IMPRINT",EDGE,{"disambiguationData":[TD([[subQ2,-1.0]])],"derivedFrom":subQ1}),1.0]])]});}
            var Q40;
            {var subQ0=sQuery(id+"F23.wireOp",EDGE,"E24.6.0");var subQ1=sQuery(id+"F23.wireOp",EDGE,"E23.right");var subQ2=makeQuery(id+"F23.imprint","INTERSECT",VERTEX,{"derivedFrom":[subQ1,subQ0]});Q40=makeQuery(id+"F23.imprint","IMPRINT",FACE,{"disambiguationData":[TD([[makeQuery(id+"F23.imprint","IMPRINT",EDGE,{"disambiguationData":[TD([[subQ2,-1.0]])],"derivedFrom":subQ1}),-1.0]])]});}
            var Q41;
            {var subQ0=sQuery(id+"F23.wireOp",EDGE,"E24.8.1");var subQ1=sQuery(id+"F23.wireOp",EDGE,"E24.5.0");var subQ2=makeQuery(id+"F23.imprint","INTERSECT",VERTEX,{"derivedFrom":[subQ1,subQ0]});Q41=makeQuery(id+"F23.imprint","IMPRINT",FACE,{"disambiguationData":[TD([[makeQuery(id+"F23.imprint","IMPRINT",EDGE,{"disambiguationData":[TD([[subQ2,-1.0]])],"derivedFrom":subQ1}),1.0]])]});}
            var Q42;
            {var subQ1=sQuery(id+"F23.wireOp",EDGE,"E23.right");var subQ3=sQuery(id+"F23.wireOp",EDGE,"E24.6.0");var subQ4=makeQuery(id+"F23.imprint","INTERSECT",VERTEX,{"derivedFrom":[subQ1,subQ3]});Q42=makeQuery(id+"F23.imprint","IMPRINT",FACE,{"disambiguationData":[TD([[makeQuery(id+"F23.imprint","IMPRINT",EDGE,{"disambiguationData":[TD([[subQ4,-1.0]])],"derivedFrom":subQ3}),-1.0]])]});}
            var Q43;
            {var subQ1=sQuery(id+"F23.wireOp",EDGE,"E24.3.1");var subQ3=sQuery(id+"F23.wireOp",EDGE,"E24.9.0");var subQ4=makeQuery(id+"F23.imprint","INTERSECT",VERTEX,{"derivedFrom":[subQ1,subQ3]});Q43=makeQuery(id+"F23.imprint","IMPRINT",FACE,{"disambiguationData":[TD([[makeQuery(id+"F23.imprint","IMPRINT",EDGE,{"disambiguationData":[TD([[subQ4,1.0]])],"derivedFrom":subQ1}),1.0]])]});}
            var Q44;
            {var subQ1=sQuery(id+"F23.wireOp",EDGE,"E23.left");var subQ3=sQuery(id+"F23.wireOp",EDGE,"E24.4.1");var subQ4=makeQuery(id+"F23.imprint","INTERSECT",VERTEX,{"derivedFrom":[subQ1,subQ3]});Q44=makeQuery(id+"F23.imprint","IMPRINT",FACE,{"disambiguationData":[TD([[makeQuery(id+"F23.imprint","IMPRINT",EDGE,{"disambiguationData":[TD([[subQ4,1.0]])],"derivedFrom":subQ1}),-1.0]])]});}
            var Q45;
            {var subQ0=sQuery(id+"F23.wireOp",EDGE,"E24.5.1");var subQ1=sQuery(id+"F23.wireOp",EDGE,"E24.1.0");var subQ2=makeQuery(id+"F23.imprint","INTERSECT",VERTEX,{"derivedFrom":[subQ1,subQ0]});Q45=makeQuery(id+"F23.imprint","IMPRINT",FACE,{"disambiguationData":[TD([[makeQuery(id+"F23.imprint","IMPRINT",EDGE,{"disambiguationData":[TD([[subQ2,-1.0]])],"derivedFrom":subQ1}),1.0]])]});}
            var Q46;
            {var subQ0=sQuery(id+"F23.wireOp",EDGE,"E24.9.1");var subQ5=sQuery(id+"F23.wireOp",EDGE,"E24.5.0");var subQ6=makeQuery(id+"F23.imprint","INTERSECT",VERTEX,{"derivedFrom":[subQ5,subQ0]});Q46=makeQuery(id+"F23.imprint","IMPRINT",FACE,{"disambiguationData":[TD([[makeQuery(id+"F23.imprint","IMPRINT",EDGE,{"disambiguationData":[TD([[subQ6,-1.0]])],"derivedFrom":subQ5}),-1.0]])]});}
            var Q47;
            {var subQ1=sQuery(id+"F23.wireOp",EDGE,"E24.4.0");var subQ3=sQuery(id+"F23.wireOp",EDGE,"E24.8.1");var subQ4=makeQuery(id+"F23.imprint","INTERSECT",VERTEX,{"derivedFrom":[subQ1,subQ3]});Q47=makeQuery(id+"F23.imprint","IMPRINT",FACE,{"disambiguationData":[TD([[makeQuery(id+"F23.imprint","IMPRINT",EDGE,{"disambiguationData":[TD([[subQ4,1.0]])],"derivedFrom":subQ1}),-1.0]])]});}
            var Q48;
            {var subQ0=sQuery(id+"F23.wireOp",EDGE,"E24.8.0");var subQ1=sQuery(id+"F23.wireOp",EDGE,"E23.right");var subQ2=makeQuery(id+"F23.imprint","INTERSECT",VERTEX,{"derivedFrom":[subQ1,subQ0]});Q48=makeQuery(id+"F23.imprint","IMPRINT",FACE,{"disambiguationData":[TD([[makeQuery(id+"F23.imprint","IMPRINT",EDGE,{"disambiguationData":[TD([[subQ2,-1.0]])],"derivedFrom":subQ1}),1.0]])]});}
            var Q49;
            {var subQ1=sQuery(id+"F23.wireOp",EDGE,"E24.5.0");var subQ3=sQuery(id+"F23.wireOp",EDGE,"E24.9.1");var subQ4=makeQuery(id+"F23.imprint","INTERSECT",VERTEX,{"derivedFrom":[subQ1,subQ3]});Q49=makeQuery(id+"F23.imprint","IMPRINT",FACE,{"disambiguationData":[TD([[makeQuery(id+"F23.imprint","IMPRINT",EDGE,{"disambiguationData":[TD([[subQ4,1.0]])],"derivedFrom":subQ1}),-1.0]])]});}
            var Q50;
            {var subQ0=sQuery(id+"F23.wireOp",EDGE,"E24.7.1");var subQ1=sQuery(id+"F23.wireOp",EDGE,"E24.4.0");var subQ2=makeQuery(id+"F23.imprint","INTERSECT",VERTEX,{"derivedFrom":[subQ1,subQ0]});Q50=makeQuery(id+"F23.imprint","IMPRINT",FACE,{"disambiguationData":[TD([[makeQuery(id+"F23.imprint","IMPRINT",EDGE,{"disambiguationData":[TD([[subQ2,-1.0]])],"derivedFrom":subQ1}),1.0]])]});}
            var Q51;
            {var subQ0=sQuery(id+"F23.wireOp",EDGE,"E24.7.0");var subQ1=sQuery(id+"F23.wireOp",EDGE,"E23.right");var subQ2=makeQuery(id+"F23.imprint","INTERSECT",VERTEX,{"derivedFrom":[subQ1,subQ0]});Q51=makeQuery(id+"F23.imprint","IMPRINT",FACE,{"disambiguationData":[TD([[makeQuery(id+"F23.imprint","IMPRINT",EDGE,{"disambiguationData":[TD([[subQ2,-1.0]])],"derivedFrom":subQ1}),-1.0]])]});}
            var Q52;
            {var subQ1=sQuery(id+"F23.wireOp",EDGE,"E24.3.0");var subQ3=sQuery(id+"F23.wireOp",EDGE,"E24.7.1");var subQ4=makeQuery(id+"F23.imprint","INTERSECT",VERTEX,{"derivedFrom":[subQ1,subQ3]});Q52=makeQuery(id+"F23.imprint","IMPRINT",FACE,{"disambiguationData":[TD([[makeQuery(id+"F23.imprint","IMPRINT",EDGE,{"disambiguationData":[TD([[subQ4,1.0]])],"derivedFrom":subQ1}),-1.0]])]});}
            var Q53;
            {var subQ0=sQuery(id+"F23.wireOp",EDGE,"E24.9.1");var subQ1=sQuery(id+"F23.wireOp",EDGE,"E24.5.0");var subQ2=makeQuery(id+"F23.imprint","INTERSECT",VERTEX,{"derivedFrom":[subQ1,subQ0]});Q53=makeQuery(id+"F23.imprint","IMPRINT",FACE,{"disambiguationData":[TD([[makeQuery(id+"F23.imprint","IMPRINT",EDGE,{"disambiguationData":[TD([[subQ2,-1.0]])],"derivedFrom":subQ1}),1.0]])]});}
            var Q54;
            {var subQ0=sQuery(id+"F23.wireOp",EDGE,"E24.4.1");var subQ1=sQuery(id+"F23.wireOp",EDGE,"E23.left");var subQ2=makeQuery(id+"F23.imprint","INTERSECT",VERTEX,{"derivedFrom":[subQ1,subQ0]});Q54=makeQuery(id+"F23.imprint","IMPRINT",FACE,{"disambiguationData":[TD([[makeQuery(id+"F23.imprint","IMPRINT",EDGE,{"disambiguationData":[TD([[subQ2,-1.0]])],"derivedFrom":subQ1}),-1.0]])]});}
            var Q55;
            {var subQ0=sQuery(id+"F23.wireOp",EDGE,"E24.7.0");var subQ1=sQuery(id+"F23.wireOp",EDGE,"E24.1.1");var subQ2=makeQuery(id+"F23.imprint","INTERSECT",VERTEX,{"derivedFrom":[subQ1,subQ0]});Q55=makeQuery(id+"F23.imprint","IMPRINT",FACE,{"disambiguationData":[TD([[makeQuery(id+"F23.imprint","IMPRINT",EDGE,{"disambiguationData":[TD([[subQ2,-1.0]])],"derivedFrom":subQ1}),1.0]])]});}
            var Q56;
            {var subQ0=sQuery(id+"F23.wireOp",EDGE,"E24.3.1");var subQ1=sQuery(id+"F23.wireOp",EDGE,"E23.left");var subQ2=makeQuery(id+"F23.imprint","INTERSECT",VERTEX,{"derivedFrom":[subQ1,subQ0]});Q56=makeQuery(id+"F23.imprint","IMPRINT",FACE,{"disambiguationData":[TD([[makeQuery(id+"F23.imprint","IMPRINT",EDGE,{"disambiguationData":[TD([[subQ2,-1.0]])],"derivedFrom":subQ1}),-1.0]])]});}
            var Q57;
            {var subQ0=sQuery(id+"F23.wireOp",EDGE,"E24.7.1");var subQ5=sQuery(id+"F23.wireOp",EDGE,"E24.3.0");var subQ7=makeQuery(id+"F23.imprint","INTERSECT",VERTEX,{"derivedFrom":[subQ5,subQ0]});Q57=makeQuery(id+"F23.imprint","IMPRINT",FACE,{"disambiguationData":[TD([[makeQuery(id+"F23.imprint","IMPRINT",EDGE,{"disambiguationData":[TD([[subQ7,-1.0]])],"derivedFrom":subQ5}),-1.0]])]});}
            var Q58;
            {var subQ0=sQuery(id+"F23.wireOp",EDGE,"E24.4.1");var subQ1=sQuery(id+"F23.wireOp",EDGE,"E23.left");var subQ2=makeQuery(id+"F23.imprint","INTERSECT",VERTEX,{"derivedFrom":[subQ1,subQ0]});Q58=makeQuery(id+"F23.imprint","IMPRINT",FACE,{"disambiguationData":[TD([[makeQuery(id+"F23.imprint","IMPRINT",EDGE,{"disambiguationData":[TD([[subQ2,-1.0]])],"derivedFrom":subQ1}),1.0]])]});}
            var Q59;
            {var subQ0=sQuery(id+"F23.wireOp",EDGE,"E24.6.0");var subQ1=sQuery(id+"F23.wireOp",EDGE,"E23.right");var subQ2=makeQuery(id+"F23.imprint","INTERSECT",VERTEX,{"derivedFrom":[subQ1,subQ0]});Q59=makeQuery(id+"F23.imprint","IMPRINT",FACE,{"disambiguationData":[TD([[makeQuery(id+"F23.imprint","IMPRINT",EDGE,{"disambiguationData":[TD([[subQ2,-1.0]])],"derivedFrom":subQ1}),1.0]])]});}
            var Q60;
            {var subQ0=sQuery(id+"F23.wireOp",EDGE,"E24.8.1");var subQ5=sQuery(id+"F23.wireOp",EDGE,"E24.4.0");var subQ6=makeQuery(id+"F23.imprint","INTERSECT",VERTEX,{"derivedFrom":[subQ5,subQ0]});Q60=makeQuery(id+"F23.imprint","IMPRINT",FACE,{"disambiguationData":[TD([[makeQuery(id+"F23.imprint","IMPRINT",EDGE,{"disambiguationData":[TD([[subQ6,-1.0]])],"derivedFrom":subQ5}),-1.0]])]});}
            var Q61;
            {var subQ0=sQuery(id+"F23.wireOp",EDGE,"E24.8.0");var subQ1=sQuery(id+"F23.wireOp",EDGE,"E24.2.1");var subQ2=makeQuery(id+"F23.imprint","INTERSECT",VERTEX,{"derivedFrom":[subQ1,subQ0]});Q61=makeQuery(id+"F23.imprint","IMPRINT",FACE,{"disambiguationData":[TD([[makeQuery(id+"F23.imprint","IMPRINT",EDGE,{"disambiguationData":[TD([[subQ2,-1.0]])],"derivedFrom":subQ1}),1.0]])]});}
            var Q62;
            {var subQ0=sQuery(id+"F23.wireOp",EDGE,"E24.4.1");var subQ1=sQuery(id+"F23.wireOp",EDGE,"E24.1.0");var subQ2=makeQuery(id+"F23.imprint","INTERSECT",VERTEX,{"derivedFrom":[subQ1,subQ0]});Q62=makeQuery(id+"F23.imprint","IMPRINT",FACE,{"disambiguationData":[TD([[makeQuery(id+"F23.imprint","IMPRINT",EDGE,{"disambiguationData":[TD([[subQ2,-1.0]])],"derivedFrom":subQ1}),1.0]])]});}
            extrude(context, id + "F24", {"entities" : qUnion([Q0, Q1, Q2, Q3, Q4, Q5, Q6, Q7, Q8, Q9, Q10, Q11, Q12, Q13, Q14, Q15, Q16, Q17, Q18, Q19, Q20, Q21, Q22, Q23, Q24, Q25, Q26, Q27, Q28, Q29, Q30, Q31, Q32, Q33, Q34, Q35, Q36, Q37, Q38, Q39, Q40, Q41, Q42, Q43, Q44, Q45, Q46, Q47, Q48, Q49, Q50, Q51, Q52, Q53, Q54, Q55, Q56, Q57, Q58, Q59, Q60, Q61, Q62]), "operationType" : NewBodyOperationType.REMOVE, "oppositeDirection" : true, "depth" : 25 * mm, "offsetDistance" : 25 * mm});
        }
        {
            var Q0;
            Q0=makeQuery(id+"F4.opLoft","CAP_FACE",FACE,{"disambiguationData":[OSD([makeQuery(id+"F3.imprint","IMPRINT",FACE,{"disambiguationData":[TD([[makeQuery(id+"F3.imprint","IMPRINT",EDGE,{"derivedFrom":sQuery(id+"F3.wireOp",EDGE,"E1.bottom")}),-1.0]])]})])],"isStart":true});
            var sketch = newSketch(context, id + "F25", { "sketchPlane" : qUnion([Q0])});
            skCircle(sketch, "E25", {"center": v(0, 0) * mm, "radius": 20 * mm});
            skSolve(sketch);
        }
        {
            var Q0;
            Q0=makeQuery(id+"F25.imprint","IMPRINT",FACE,{"disambiguationData":[TD([[makeQuery(id+"F25.imprint","IMPRINT",EDGE,{"derivedFrom":sQuery(id+"F25.wireOp",EDGE,"E25")}),1.0]])]});
            extrude(context, id + "F26", {"entities" : qUnion([Q0]), "operationType" : NewBodyOperationType.REMOVE, "oppositeDirection" : true, "depth" : 5 * mm, "offsetDistance" : 25 * mm});
        }
        {
            var Q0;
            Q0=makeQuery(id+"F4.opLoft","MID_CAP_EDGE",EDGE,{"disambiguationData":[OSD([sQuery(id+"F3.wireOp",EDGE,"E1.top"),sQuery(id+"F3.wireOp",EDGE,"E1.left"),sQuery(id+"F3.wireOp",EDGE,"E1.right")])],"capPos":1.0});
            var Q1;
            Q1=makeQuery(id+"F4.opLoft","MID_CAP_EDGE",EDGE,{"disambiguationData":[OSD([sQuery(id+"F3.wireOp",EDGE,"E1.bottom"),sQuery(id+"F3.wireOp",EDGE,"E1.top"),sQuery(id+"F3.wireOp",EDGE,"E1.right")])],"capPos":1.0});
            var Q2;
            Q2=makeQuery(id+"F4.opLoft","MID_CAP_EDGE",EDGE,{"disambiguationData":[OSD([sQuery(id+"F3.wireOp",EDGE,"E1.bottom"),sQuery(id+"F3.wireOp",EDGE,"E1.left"),sQuery(id+"F3.wireOp",EDGE,"E1.right")])],"capPos":1.0});
            var Q3;
            Q3=makeQuery(id+"F4.opLoft","MID_CAP_EDGE",EDGE,{"disambiguationData":[OSD([sQuery(id+"F3.wireOp",EDGE,"E1.bottom"),sQuery(id+"F3.wireOp",EDGE,"E1.top"),sQuery(id+"F3.wireOp",EDGE,"E1.left")])],"capPos":1.0});
            var Q4;
            Q4=makeQuery(id+"F4.opLoft","SWEPT_EDGE",EDGE,{"disambiguationData":[OSD([sQuery(id+"F0.wireOp",EDGE,"E0.top"),sQuery(id+"F0.wireOp",EDGE,"E0.left"),sQuery(id+"F3.wireOp",EDGE,"E1.top"),sQuery(id+"F3.wireOp",EDGE,"E1.left")])]});
            var Q5;
            Q5=makeQuery(id+"F4.opLoft","SWEPT_EDGE",EDGE,{"disambiguationData":[OSD([sQuery(id+"F0.wireOp",EDGE,"E0.top"),sQuery(id+"F0.wireOp",EDGE,"E0.right"),sQuery(id+"F3.wireOp",EDGE,"E1.top"),sQuery(id+"F3.wireOp",EDGE,"E1.right")])]});
            var Q6;
            Q6=makeQuery(id+"F4.opLoft","SWEPT_EDGE",EDGE,{"disambiguationData":[OSD([sQuery(id+"F0.wireOp",EDGE,"E0.bottom"),sQuery(id+"F0.wireOp",EDGE,"E0.left"),sQuery(id+"F3.wireOp",EDGE,"E1.bottom"),sQuery(id+"F3.wireOp",EDGE,"E1.left")])]});
            var Q7;
            Q7=makeQuery(id+"F4.opLoft","SWEPT_EDGE",EDGE,{"disambiguationData":[OSD([sQuery(id+"F0.wireOp",EDGE,"E0.bottom"),sQuery(id+"F0.wireOp",EDGE,"E0.right"),sQuery(id+"F3.wireOp",EDGE,"E1.bottom"),sQuery(id+"F3.wireOp",EDGE,"E1.right")])]});
            fillet(context, id + "F27", {"entities" : qUnion([Q0, Q1, Q2, Q3, Q4, Q5, Q6, Q7]), "radius" : 5 * mm, "tangentPropagation" : true, "allowEdgeOverflow" : false});
        }
        {
            var Q0;
            Q0=makeQuery(id+"F26.boolean.opBoolean","COPY",FACE,{"derivedFrom":makeQuery(id+"F26.opExtrude","CAP_FACE",FACE,{"disambiguationData":[OSD([sQuery(id+"F25.wireOp",EDGE,"E25")])],"isStart":false})});
            var sketch = newSketch(context, id + "F28", { "sketchPlane" : qUnion([Q0])});
            skCircle(sketch, "E26", {"center": v(0, 0) * mm, "radius": 1.8 * mm});
            skSolve(sketch);
        }
        {
            var Q0;
            Q0=makeQuery(id+"F28.imprint","IMPRINT",FACE,{"disambiguationData":[TD([[makeQuery(id+"F28.imprint","IMPRINT",EDGE,{"derivedFrom":sQuery(id+"F28.wireOp",EDGE,"E26")}),1.0]])]});
            extrude(context, id + "F29", {"entities" : qUnion([Q0]), "operationType" : NewBodyOperationType.REMOVE, "oppositeDirection" : true, "depth" : 11 * mm, "offsetDistance" : 25 * mm});
        }
        {
            var Q0;
            Q0=makeQuery(id+"F6.boolean.opBoolean","COPY",FACE,{"derivedFrom":makeQuery(id+"F6.opExtrude","CAP_FACE",FACE,{"disambiguationData":[OSD([sQuery(id+"F5.wireOp",EDGE,"E4.bottom"),sQuery(id+"F5.wireOp",EDGE,"E4.top"),sQuery(id+"F5.wireOp",EDGE,"E4.left"),sQuery(id+"F5.wireOp",EDGE,"E4.right")])],"isStart":false})});
            var sketch = newSketch(context, id + "F30", { "sketchPlane" : qUnion([Q0])});
            skLineSegment(sketch, "E27.bottom", {"start": v(-50, 24.75) * mm, "end": v(-57.5, 24.75) * mm});
            skLineSegment(sketch, "E27.top", {"start": v(-50, -24.75) * mm, "end": v(-57.5, -24.75) * mm});
            skLineSegment(sketch, "E27.left", {"start": v(-50, 24.75) * mm, "end": v(-50, -24.75) * mm});
            skLineSegment(sketch, "E27.right", {"start": v(-57.5, 24.75) * mm, "end": v(-57.5, -24.75) * mm});
            skSolve(sketch);
        }
        {
            var Q0;
            Q0=makeQuery(id+"F30.imprint","IMPRINT",FACE,{"disambiguationData":[TD([[makeQuery(id+"F30.imprint","IMPRINT",EDGE,{"derivedFrom":sQuery(id+"F30.wireOp",EDGE,"E27.bottom")}),1.0]])]});
            extrude(context, id + "F31", {"entities" : qUnion([Q0]), "operationType" : NewBodyOperationType.REMOVE, "oppositeDirection" : true, "depth" : 23.5 * mm, "offsetDistance" : 25 * mm});
        }
        {
            var Q0;
            Q0=makeQuery(id+"F6.boolean.opBoolean","COPY",FACE,{"derivedFrom":makeQuery(id+"F6.opExtrude","CAP_FACE",FACE,{"disambiguationData":[OSD([sQuery(id+"F5.wireOp",EDGE,"E5.bottom"),sQuery(id+"F5.wireOp",EDGE,"E5.top"),sQuery(id+"F5.wireOp",EDGE,"E5.left"),sQuery(id+"F5.wireOp",EDGE,"E5.right")])],"isStart":false})});
            var sketch = newSketch(context, id + "F32", { "sketchPlane" : qUnion([Q0])});
            skLineSegment(sketch, "E28.bottom", {"start": v(50, -24.75) * mm, "end": v(57.5, -24.75) * mm});
            skLineSegment(sketch, "E28.top", {"start": v(50, 24.75) * mm, "end": v(57.5, 24.75) * mm});
            skLineSegment(sketch, "E28.left", {"start": v(50, -24.75) * mm, "end": v(50, 24.75) * mm});
            skLineSegment(sketch, "E28.right", {"start": v(57.5, -24.75) * mm, "end": v(57.5, 24.75) * mm});
            skSolve(sketch);
        }
        {
            var Q0;
            Q0=makeQuery(id+"F32.imprint","IMPRINT",FACE,{"disambiguationData":[TD([[makeQuery(id+"F32.imprint","IMPRINT",EDGE,{"derivedFrom":sQuery(id+"F32.wireOp",EDGE,"E28.bottom")}),-1.0]])]});
            extrude(context, id + "F33", {"entities" : qUnion([Q0]), "operationType" : NewBodyOperationType.REMOVE, "oppositeDirection" : true, "depth" : 23.5 * mm, "offsetDistance" : 25 * mm});
        }
    });
